annotation { "Feature Type Name" : "Feature", "Feature Type Description" : "" }
export const myFeature = defineFeature(function(context is Context, id is Id, definition is map)
    precondition{}
    {
        {
            var Q0;
            Q0=qCreatedBy(makeId("Front.planeOp"),FACE);
            var sketch = newSketch(context, id + "F0", { "sketchPlane" : qUnion([Q0])});
            skLineSegment(sketch, "E0.bottom", {"start": v(107, -79) * mm, "end": v(-107, -79) * mm});
            skLineSegment(sketch, "E0.top", {"start": v(107, 79) * mm, "end": v(-107, 79) * mm});
            skLineSegment(sketch, "E0.left", {"start": v(107, -79) * mm, "end": v(107, 79) * mm});
            skLineSegment(sketch, "E0.right", {"start": v(-107, -79) * mm, "end": v(-107, 79) * mm});
            skPoint(sketch, "E0.middle", {"position": v(0, 0) * mm});
            skSolve(sketch);
        }
        {
            var Q0;
            Q0=makeQuery(id+"F0.imprint","IMPRINT",FACE,{"disambiguationData":[TD([[makeQuery(id+"F0.imprint","IMPRINT",EDGE,{"derivedFrom":sQuery(id+"F0.wireOp",EDGE,"E0.bottom")}),-1.0]])]});
            extrude(context, id + "F1", {"entities" : qUnion([Q0]), "oppositeDirection" : true, "depth" : 6.2 * mm, "offsetDistance" : 25 * mm});
        }
        {
            var Q0;
            Q0=makeQuery(id+"F1.opExtrude","CAP_FACE",FACE,{"disambiguationData":[OSD([sQuery(id+"F0.wireOp",EDGE,"E0.bottom"),sQuery(id+"F0.wireOp",EDGE,"E0.top"),sQuery(id+"F0.wireOp",EDGE,"E0.left"),sQuery(id+"F0.wireOp",EDGE,"E0.right")])],"isStart":true});
            var sketch = newSketch(context, id + "F2", { "sketchPlane" : qUnion([Q0])});
            skLineSegment(sketch, "E1.bottom", {"start": v(98, -70) * mm, "end": v(-98, -70) * mm});
            skLineSegment(sketch, "E1.top", {"start": v(98, 70) * mm, "end": v(-98, 70) * mm});
            skLineSegment(sketch, "E1.left", {"start": v(98, -70) * mm, "end": v(98, 70) * mm});
            skLineSegment(sketch, "E1.right", {"start": v(-98, -70) * mm, "end": v(-98, 70) * mm});
            skPoint(sketch, "E1.middle", {"position": v(0, 0) * mm});
            skSolve(sketch);
        }
        {
            var Q0;
            Q0=makeQuery(id+"F2.imprint","IMPRINT",FACE,{"disambiguationData":[TD([[makeQuery(id+"F2.imprint","IMPRINT",EDGE,{"derivedFrom":sQuery(id+"F2.wireOp",EDGE,"E1.bottom")}),-1.0]])]});
            extrude(context, id + "F3", {"entities" : qUnion([Q0]), "operationType" : NewBodyOperationType.ADD, "depth" : 44 * mm, "offsetDistance" : 25 * mm});
        }
        {
            var Q0;
            Q0=makeQuery(id+"F1.opExtrude","SWEPT_FACE",FACE,{"disambiguationData":[OSD([sQuery(id+"F0.wireOp",EDGE,"E0.top")])]});
            var sketch = newSketch(context, id + "F4", { "sketchPlane" : qUnion([Q0])});
            skLineSegment(sketch, "E2", {"start": v(107, 0) * mm, "end": v(107, 0) * mm});
            skLineSegment(sketch, "E3", {"start": v(100.8, 6.2) * mm, "end": v(96.38, 6.2) * mm});
            skPoint(sketch, "E4.visualSharp", {"position": v(107, 6.2) * mm});
            skArc(sketch, "E4.filletArc", {"start": v(107, 0) * mm, "mid": v(105.18, 4.38) * mm, "end": v(100.8, 6.2) * mm});
            skLineSegment(sketch, "E5", {"start": v(96.38, 6.2) * mm, "end": v(-100.8, 6.2) * mm});
            skLineSegment(sketch, "E6", {"start": v(-107, 0) * mm, "end": v(-107, 0) * mm});
            skLineSegment(sketch, "E7", {"start": v(-107, 0) * mm, "end": v(107, 0) * mm});
            skPoint(sketch, "E8.visualSharp", {"position": v(-107, 6.2) * mm});
            skArc(sketch, "E8.filletArc", {"start": v(-100.8, 6.2) * mm, "mid": v(-105.18, 4.38) * mm, "end": v(-107, 0) * mm});
            skSolve(sketch);
        }
        {
            var Q0;
            {var subQ0=sQuery(id+"F4.wireOp",EDGE,"E4.filletArc");Q0=makeQuery(id+"F4.imprint","IMPRINT",FACE,{"disambiguationData":[TD([[makeQuery(id+"F4.imprint","IMPRINT",EDGE,{"derivedFrom":subQ0}),-1.0]])]});}
            var Q1;
            {var subQ0=sQuery(id+"F4.wireOp",EDGE,"E8.filletArc");Q1=makeQuery(id+"F4.imprint","IMPRINT",FACE,{"disambiguationData":[TD([[makeQuery(id+"F4.imprint","IMPRINT",EDGE,{"derivedFrom":subQ0}),-1.0]])]});}
            extrude(context, id + "F5", {"entities" : qUnion([Q0, Q1]), "operationType" : NewBodyOperationType.REMOVE, "oppositeDirection" : true, "depth" : 158 * mm, "offsetDistance" : 25 * mm});
        }
        {
            var Q0;
            Q0=makeQuery(id+"F3.opExtrude","CAP_FACE",FACE,{"disambiguationData":[OSD([sQuery(id+"F2.wireOp",EDGE,"E1.bottom"),sQuery(id+"F2.wireOp",EDGE,"E1.top"),sQuery(id+"F2.wireOp",EDGE,"E1.left"),sQuery(id+"F2.wireOp",EDGE,"E1.right")])],"isStart":false});
            var sketch = newSketch(context, id + "F6", { "sketchPlane" : qUnion([Q0])});
            skLineSegment(sketch, "E9.bottom", {"start": v(98, -70) * mm, "end": v(-98, -70) * mm});
            skLineSegment(sketch, "E9.top", {"start": v(98, 40) * mm, "end": v(-98, 40) * mm});
            skLineSegment(sketch, "E9.left", {"start": v(98, -70) * mm, "end": v(98, 40) * mm});
            skLineSegment(sketch, "E9.right", {"start": v(-98, -70) * mm, "end": v(-98, 40) * mm});
            skSolve(sketch);
        }
        {
            var Q0;
            Q0=makeQuery(id+"F6.imprint","IMPRINT",FACE,{"disambiguationData":[TD([[makeQuery(id+"F6.imprint","IMPRINT",EDGE,{"derivedFrom":sQuery(id+"F6.wireOp",EDGE,"E9.bottom")}),-1.0]])]});
            extrude(context, id + "F7", {"entities" : qUnion([Q0]), "operationType" : NewBodyOperationType.ADD, "depth" : 20 * mm, "offsetDistance" : 25 * mm});
        }
        {
            var Q0;
            Q0=makeQuery(id+"F7.boolean.opBoolean","MERGE",EDGE,{"derivedFrom":[makeQuery(id+"F3.opExtrude","SWEPT_EDGE",EDGE,{"disambiguationData":[OSD([sQuery(id+"F2.wireOp",EDGE,"E1.bottom"),sQuery(id+"F2.wireOp",EDGE,"E1.right")])]}),makeQuery(id+"F7.opExtrude","SWEPT_EDGE",EDGE,{"disambiguationData":[OSD([sQuery(id+"F6.wireOp",EDGE,"E9.bottom"),sQuery(id+"F6.wireOp",EDGE,"E9.right")])]})]});
            var Q1;
            Q1=makeQuery(id+"F7.boolean.opBoolean","MERGE",EDGE,{"derivedFrom":[makeQuery(id+"F3.opExtrude","SWEPT_EDGE",EDGE,{"disambiguationData":[OSD([sQuery(id+"F2.wireOp",EDGE,"E1.bottom"),sQuery(id+"F2.wireOp",EDGE,"E1.left")])]}),makeQuery(id+"F7.opExtrude","SWEPT_EDGE",EDGE,{"disambiguationData":[OSD([sQuery(id+"F6.wireOp",EDGE,"E9.bottom"),sQuery(id+"F6.wireOp",EDGE,"E9.left")])]})]});
            var Q2;
            Q2=makeQuery(id+"F3.opExtrude","SWEPT_EDGE",EDGE,{"disambiguationData":[OSD([sQuery(id+"F2.wireOp",EDGE,"E1.top"),sQuery(id+"F2.wireOp",EDGE,"E1.left")])]});
            var Q3;
            Q3=makeQuery(id+"F7.opExtrude","SWEPT_EDGE",EDGE,{"disambiguationData":[OSD([sQuery(id+"F2.wireOp",EDGE,"E1.left"),sQuery(id+"F6.wireOp",EDGE,"E9.top"),sQuery(id+"F6.wireOp",EDGE,"E9.left")])]});
            var Q4;
            Q4=makeQuery(id+"F3.opExtrude","SWEPT_EDGE",EDGE,{"disambiguationData":[OSD([sQuery(id+"F2.wireOp",EDGE,"E1.top"),sQuery(id+"F2.wireOp",EDGE,"E1.right")])]});
            var Q5;
            Q5=makeQuery(id+"F7.opExtrude","SWEPT_EDGE",EDGE,{"disambiguationData":[OSD([sQuery(id+"F2.wireOp",EDGE,"E1.right"),sQuery(id+"F6.wireOp",EDGE,"E9.top"),sQuery(id+"F6.wireOp",EDGE,"E9.right")])]});
            fillet(context, id + "F8", {"entities" : qUnion([Q0, Q1, Q2, Q3, Q4, Q5]), "radius" : 5 * mm, "tangentPropagation" : true, "allowEdgeOverflow" : false});
        }
        {
            var Q0;
            Q0=makeQuery(id+"F7.boolean.opBoolean","MERGE",FACE,{"derivedFrom":[makeQuery(id+"F3.opExtrude","SWEPT_FACE",FACE,{"disambiguationData":[OSD([sQuery(id+"F2.wireOp",EDGE,"E1.right")])]}),makeQuery(id+"F7.opExtrude","SWEPT_FACE",FACE,{"disambiguationData":[OSD([sQuery(id+"F6.wireOp",EDGE,"E9.right")])]})]});
            var sketch = newSketch(context, id + "F9", { "sketchPlane" : qUnion([Q0])});
            skLineSegment(sketch, "E10.bottom", {"start": v(7.5, -58) * mm, "end": v(19.5, -58) * mm});
            skLineSegment(sketch, "E10.top", {"start": v(7.5, -54) * mm, "end": v(19.5, -54) * mm});
            skLineSegment(sketch, "E10.left", {"start": v(7.5, -58) * mm, "end": v(7.5, -54) * mm});
            skLineSegment(sketch, "E10.right", {"start": v(19.5, -58) * mm, "end": v(19.5, -54) * mm});
            skLineSegment(sketch, "E11.0.1.0", {"start": v(7.5, -47) * mm, "end": v(19.5, -47) * mm});
            skLineSegment(sketch, "E11.0.1.1", {"start": v(7.5, -51) * mm, "end": v(19.5, -51) * mm});
            skLineSegment(sketch, "E11.0.1.2", {"start": v(19.5, -51) * mm, "end": v(19.5, -47) * mm});
            skLineSegment(sketch, "E11.0.1.3", {"start": v(7.5, -51) * mm, "end": v(7.5, -47) * mm});
            skLineSegment(sketch, "E11.0.2.0", {"start": v(7.5, -40) * mm, "end": v(19.5, -40) * mm});
            skLineSegment(sketch, "E11.0.2.1", {"start": v(7.5, -44) * mm, "end": v(19.5, -44) * mm});
            skLineSegment(sketch, "E11.0.2.2", {"start": v(19.5, -44) * mm, "end": v(19.5, -40) * mm});
            skLineSegment(sketch, "E11.0.2.3", {"start": v(7.5, -44) * mm, "end": v(7.5, -40) * mm});
            skLineSegment(sketch, "E11.0.3.0", {"start": v(7.5, -33) * mm, "end": v(19.5, -33) * mm});
            skLineSegment(sketch, "E11.0.3.1", {"start": v(7.5, -37) * mm, "end": v(19.5, -37) * mm});
            skLineSegment(sketch, "E11.0.3.2", {"start": v(19.5, -37) * mm, "end": v(19.5, -33) * mm});
            skLineSegment(sketch, "E11.0.3.3", {"start": v(7.5, -37) * mm, "end": v(7.5, -33) * mm});
            skLineSegment(sketch, "E11.0.4.0", {"start": v(7.5, -26) * mm, "end": v(19.5, -26) * mm});
            skLineSegment(sketch, "E11.0.4.1", {"start": v(7.5, -30) * mm, "end": v(19.5, -30) * mm});
            skLineSegment(sketch, "E11.0.4.2", {"start": v(19.5, -30) * mm, "end": v(19.5, -26) * mm});
            skLineSegment(sketch, "E11.0.4.3", {"start": v(7.5, -30) * mm, "end": v(7.5, -26) * mm});
            skLineSegment(sketch, "E11.0.5.0", {"start": v(7.5, -19) * mm, "end": v(19.5, -19) * mm});
            skLineSegment(sketch, "E11.0.5.1", {"start": v(7.5, -23) * mm, "end": v(19.5, -23) * mm});
            skLineSegment(sketch, "E11.0.5.2", {"start": v(19.5, -23) * mm, "end": v(19.5, -19) * mm});
            skLineSegment(sketch, "E11.0.5.3", {"start": v(7.5, -23) * mm, "end": v(7.5, -19) * mm});
            skLineSegment(sketch, "E11.0.6.0", {"start": v(7.5, -12) * mm, "end": v(19.5, -12) * mm});
            skLineSegment(sketch, "E11.0.6.1", {"start": v(7.5, -16) * mm, "end": v(19.5, -16) * mm});
            skLineSegment(sketch, "E11.0.6.2", {"start": v(19.5, -16) * mm, "end": v(19.5, -12) * mm});
            skLineSegment(sketch, "E11.0.6.3", {"start": v(7.5, -16) * mm, "end": v(7.5, -12) * mm});
            skLineSegment(sketch, "E11.0.7.0", {"start": v(7.5, -5) * mm, "end": v(19.5, -5) * mm});
            skLineSegment(sketch, "E11.0.7.1", {"start": v(7.5, -9) * mm, "end": v(19.5, -9) * mm});
            skLineSegment(sketch, "E11.0.7.2", {"start": v(19.5, -9) * mm, "end": v(19.5, -5) * mm});
            skLineSegment(sketch, "E11.0.7.3", {"start": v(7.5, -9) * mm, "end": v(7.5, -5) * mm});
            skLineSegment(sketch, "E11.0.8.0", {"start": v(7.5, 2) * mm, "end": v(19.5, 2) * mm});
            skLineSegment(sketch, "E11.0.8.1", {"start": v(7.5, -2) * mm, "end": v(19.5, -2) * mm});
            skLineSegment(sketch, "E11.0.8.2", {"start": v(19.5, -2) * mm, "end": v(19.5, 2) * mm});
            skLineSegment(sketch, "E11.0.8.3", {"start": v(7.5, -2) * mm, "end": v(7.5, 2) * mm});
            skLineSegment(sketch, "E11.0.9.0", {"start": v(7.5, 9) * mm, "end": v(19.5, 9) * mm});
            skLineSegment(sketch, "E11.0.9.1", {"start": v(7.5, 5) * mm, "end": v(19.5, 5) * mm});
            skLineSegment(sketch, "E11.0.9.2", {"start": v(19.5, 5) * mm, "end": v(19.5, 9) * mm});
            skLineSegment(sketch, "E11.0.9.3", {"start": v(7.5, 5) * mm, "end": v(7.5, 9) * mm});
            skLineSegment(sketch, "E11.0.10.0", {"start": v(7.5, 16) * mm, "end": v(19.5, 16) * mm});
            skLineSegment(sketch, "E11.0.10.1", {"start": v(7.5, 12) * mm, "end": v(19.5, 12) * mm});
            skLineSegment(sketch, "E11.0.10.2", {"start": v(19.5, 12) * mm, "end": v(19.5, 16) * mm});
            skLineSegment(sketch, "E11.0.10.3", {"start": v(7.5, 12) * mm, "end": v(7.5, 16) * mm});
            skLineSegment(sketch, "E11.0.11.0", {"start": v(7.5, 23) * mm, "end": v(19.5, 23) * mm});
            skLineSegment(sketch, "E11.0.11.1", {"start": v(7.5, 19) * mm, "end": v(19.5, 19) * mm});
            skLineSegment(sketch, "E11.0.11.2", {"start": v(19.5, 19) * mm, "end": v(19.5, 23) * mm});
            skLineSegment(sketch, "E11.0.11.3", {"start": v(7.5, 19) * mm, "end": v(7.5, 23) * mm});
            skLineSegment(sketch, "E11.0.13.0", {"start": v(7.5, 37) * mm, "end": v(19.5, 37) * mm});
            skLineSegment(sketch, "E11.0.13.1", {"start": v(7.5, 33) * mm, "end": v(19.5, 33) * mm});
            skLineSegment(sketch, "E11.0.13.2", {"start": v(19.5, 33) * mm, "end": v(19.5, 37) * mm});
            skLineSegment(sketch, "E11.0.13.3", {"start": v(7.5, 33) * mm, "end": v(7.5, 37) * mm});
            skLineSegment(sketch, "E11.0.14.0", {"start": v(7.5, 44) * mm, "end": v(19.5, 44) * mm});
            skLineSegment(sketch, "E11.0.14.1", {"start": v(7.5, 40) * mm, "end": v(19.5, 40) * mm});
            skLineSegment(sketch, "E11.0.14.2", {"start": v(19.5, 40) * mm, "end": v(19.5, 44) * mm});
            skLineSegment(sketch, "E11.0.14.3", {"start": v(7.5, 40) * mm, "end": v(7.5, 44) * mm});
            skLineSegment(sketch, "E11.0.15.0", {"start": v(7.5, 51) * mm, "end": v(19.5, 51) * mm});
            skLineSegment(sketch, "E11.0.15.1", {"start": v(7.5, 47) * mm, "end": v(19.5, 47) * mm});
            skLineSegment(sketch, "E11.0.15.2", {"start": v(19.5, 47) * mm, "end": v(19.5, 51) * mm});
            skLineSegment(sketch, "E11.0.15.3", {"start": v(7.5, 47) * mm, "end": v(7.5, 51) * mm});
            skLineSegment(sketch, "E11.0.16.0", {"start": v(7.5, 58) * mm, "end": v(19.5, 58) * mm});
            skLineSegment(sketch, "E11.0.16.1", {"start": v(7.5, 54) * mm, "end": v(19.5, 54) * mm});
            skLineSegment(sketch, "E11.0.16.2", {"start": v(19.5, 54) * mm, "end": v(19.5, 58) * mm});
            skLineSegment(sketch, "E11.0.16.3", {"start": v(7.5, 54) * mm, "end": v(7.5, 58) * mm});
            skLineSegment(sketch, "E11.1.0.0", {"start": v(24.5, -54) * mm, "end": v(36.5, -54) * mm});
            skLineSegment(sketch, "E11.1.0.1", {"start": v(24.5, -58) * mm, "end": v(36.5, -58) * mm});
            skLineSegment(sketch, "E11.1.0.2", {"start": v(36.5, -58) * mm, "end": v(36.5, -54) * mm});
            skLineSegment(sketch, "E11.1.0.3", {"start": v(24.5, -58) * mm, "end": v(24.5, -54) * mm});
            skLineSegment(sketch, "E11.1.1.0", {"start": v(24.5, -47) * mm, "end": v(36.5, -47) * mm});
            skLineSegment(sketch, "E11.1.1.1", {"start": v(24.5, -51) * mm, "end": v(36.5, -51) * mm});
            skLineSegment(sketch, "E11.1.1.2", {"start": v(36.5, -51) * mm, "end": v(36.5, -47) * mm});
            skLineSegment(sketch, "E11.1.1.3", {"start": v(24.5, -51) * mm, "end": v(24.5, -47) * mm});
            skLineSegment(sketch, "E11.1.2.0", {"start": v(24.5, -40) * mm, "end": v(36.5, -40) * mm});
            skLineSegment(sketch, "E11.1.2.1", {"start": v(24.5, -44) * mm, "end": v(36.5, -44) * mm});
            skLineSegment(sketch, "E11.1.2.2", {"start": v(36.5, -44) * mm, "end": v(36.5, -40) * mm});
            skLineSegment(sketch, "E11.1.2.3", {"start": v(24.5, -44) * mm, "end": v(24.5, -40) * mm});
            skLineSegment(sketch, "E11.1.3.0", {"start": v(24.5, -33) * mm, "end": v(36.5, -33) * mm});
            skLineSegment(sketch, "E11.1.3.1", {"start": v(24.5, -37) * mm, "end": v(36.5, -37) * mm});
            skLineSegment(sketch, "E11.1.3.2", {"start": v(36.5, -37) * mm, "end": v(36.5, -33) * mm});
            skLineSegment(sketch, "E11.1.3.3", {"start": v(24.5, -37) * mm, "end": v(24.5, -33) * mm});
            skLineSegment(sketch, "E11.1.4.0", {"start": v(24.5, -26) * mm, "end": v(36.5, -26) * mm});
            skLineSegment(sketch, "E11.1.4.1", {"start": v(24.5, -30) * mm, "end": v(36.5, -30) * mm});
            skLineSegment(sketch, "E11.1.4.2", {"start": v(36.5, -30) * mm, "end": v(36.5, -26) * mm});
            skLineSegment(sketch, "E11.1.4.3", {"start": v(24.5, -30) * mm, "end": v(24.5, -26) * mm});
            skLineSegment(sketch, "E11.1.5.0", {"start": v(24.5, -19) * mm, "end": v(36.5, -19) * mm});
            skLineSegment(sketch, "E11.1.5.1", {"start": v(24.5, -23) * mm, "end": v(36.5, -23) * mm});
            skLineSegment(sketch, "E11.1.5.2", {"start": v(36.5, -23) * mm, "end": v(36.5, -19) * mm});
            skLineSegment(sketch, "E11.1.5.3", {"start": v(24.5, -23) * mm, "end": v(24.5, -19) * mm});
            skLineSegment(sketch, "E11.1.6.0", {"start": v(24.5, -12) * mm, "end": v(36.5, -12) * mm});
            skLineSegment(sketch, "E11.1.6.1", {"start": v(24.5, -16) * mm, "end": v(36.5, -16) * mm});
            skLineSegment(sketch, "E11.1.6.2", {"start": v(36.5, -16) * mm, "end": v(36.5, -12) * mm});
            skLineSegment(sketch, "E11.1.6.3", {"start": v(24.5, -16) * mm, "end": v(24.5, -12) * mm});
            skLineSegment(sketch, "E11.1.7.0", {"start": v(24.5, -5) * mm, "end": v(36.5, -5) * mm});
            skLineSegment(sketch, "E11.1.7.1", {"start": v(24.5, -9) * mm, "end": v(36.5, -9) * mm});
            skLineSegment(sketch, "E11.1.7.2", {"start": v(36.5, -9) * mm, "end": v(36.5, -5) * mm});
            skLineSegment(sketch, "E11.1.7.3", {"start": v(24.5, -9) * mm, "end": v(24.5, -5) * mm});
            skLineSegment(sketch, "E11.1.8.0", {"start": v(24.5, 2) * mm, "end": v(36.5, 2) * mm});
            skLineSegment(sketch, "E11.1.8.1", {"start": v(24.5, -2) * mm, "end": v(36.5, -2) * mm});
            skLineSegment(sketch, "E11.1.8.2", {"start": v(36.5, -2) * mm, "end": v(36.5, 2) * mm});
            skLineSegment(sketch, "E11.1.8.3", {"start": v(24.5, -2) * mm, "end": v(24.5, 2) * mm});
            skLineSegment(sketch, "E11.1.9.0", {"start": v(24.5, 9) * mm, "end": v(36.5, 9) * mm});
            skLineSegment(sketch, "E11.1.9.1", {"start": v(24.5, 5) * mm, "end": v(36.5, 5) * mm});
            skLineSegment(sketch, "E11.1.9.2", {"start": v(36.5, 5) * mm, "end": v(36.5, 9) * mm});
            skLineSegment(sketch, "E11.1.9.3", {"start": v(24.5, 5) * mm, "end": v(24.5, 9) * mm});
            skLineSegment(sketch, "E11.1.10.0", {"start": v(24.5, 16) * mm, "end": v(36.5, 16) * mm});
            skLineSegment(sketch, "E11.1.10.1", {"start": v(24.5, 12) * mm, "end": v(36.5, 12) * mm});
            skLineSegment(sketch, "E11.1.10.2", {"start": v(36.5, 12) * mm, "end": v(36.5, 16) * mm});
            skLineSegment(sketch, "E11.1.10.3", {"start": v(24.5, 12) * mm, "end": v(24.5, 16) * mm});
            skLineSegment(sketch, "E11.1.11.0", {"start": v(24.5, 23) * mm, "end": v(36.5, 23) * mm});
            skLineSegment(sketch, "E11.1.11.1", {"start": v(24.5, 19) * mm, "end": v(36.5, 19) * mm});
            skLineSegment(sketch, "E11.1.11.2", {"start": v(36.5, 19) * mm, "end": v(36.5, 23) * mm});
            skLineSegment(sketch, "E11.1.11.3", {"start": v(24.5, 19) * mm, "end": v(24.5, 23) * mm});
            skLineSegment(sketch, "E11.1.13.0", {"start": v(24.5, 37) * mm, "end": v(36.5, 37) * mm});
            skLineSegment(sketch, "E11.1.13.1", {"start": v(24.5, 33) * mm, "end": v(36.5, 33) * mm});
            skLineSegment(sketch, "E11.1.13.2", {"start": v(36.5, 33) * mm, "end": v(36.5, 37) * mm});
            skLineSegment(sketch, "E11.1.13.3", {"start": v(24.5, 33) * mm, "end": v(24.5, 37) * mm});
            skLineSegment(sketch, "E11.1.14.0", {"start": v(24.5, 44) * mm, "end": v(36.5, 44) * mm});
            skLineSegment(sketch, "E11.1.14.1", {"start": v(24.5, 40) * mm, "end": v(36.5, 40) * mm});
            skLineSegment(sketch, "E11.1.14.2", {"start": v(36.5, 40) * mm, "end": v(36.5, 44) * mm});
            skLineSegment(sketch, "E11.1.14.3", {"start": v(24.5, 40) * mm, "end": v(24.5, 44) * mm});
            skLineSegment(sketch, "E11.1.15.0", {"start": v(24.5, 51) * mm, "end": v(36.5, 51) * mm});
            skLineSegment(sketch, "E11.1.15.1", {"start": v(24.5, 47) * mm, "end": v(36.5, 47) * mm});
            skLineSegment(sketch, "E11.1.15.2", {"start": v(36.5, 47) * mm, "end": v(36.5, 51) * mm});
            skLineSegment(sketch, "E11.1.15.3", {"start": v(24.5, 47) * mm, "end": v(24.5, 51) * mm});
            skLineSegment(sketch, "E11.1.16.0", {"start": v(24.5, 58) * mm, "end": v(36.5, 58) * mm});
            skLineSegment(sketch, "E11.1.16.1", {"start": v(24.5, 54) * mm, "end": v(36.5, 54) * mm});
            skLineSegment(sketch, "E11.1.16.2", {"start": v(36.5, 54) * mm, "end": v(36.5, 58) * mm});
            skLineSegment(sketch, "E11.1.16.3", {"start": v(24.5, 54) * mm, "end": v(24.5, 58) * mm});
            skLineSegment(sketch, "E11.direction1", {"start": v(7.5, -54) * mm, "end": v(24.5, -54) * mm, "construction": true});
            skLineSegment(sketch, "E11.direction2", {"start": v(7.5, -54) * mm, "end": v(7.5, -47) * mm, "construction": true});
            skSolve(sketch);
        }
        {
            var Q0;
            Q0=makeQuery(id+"F9.imprint","IMPRINT",FACE,{"disambiguationData":[TD([[makeQuery(id+"F9.imprint","IMPRINT",EDGE,{"derivedFrom":sQuery(id+"F9.wireOp",EDGE,"E10.bottom")}),1.0]])]});
            var Q1;
            Q1=makeQuery(id+"F9.imprint","IMPRINT",FACE,{"disambiguationData":[TD([[makeQuery(id+"F9.imprint","IMPRINT",EDGE,{"derivedFrom":sQuery(id+"F9.wireOp",EDGE,"E11.0.1.0")}),-1.0]])]});
            var Q2;
            Q2=makeQuery(id+"F9.imprint","IMPRINT",FACE,{"disambiguationData":[TD([[makeQuery(id+"F9.imprint","IMPRINT",EDGE,{"derivedFrom":sQuery(id+"F9.wireOp",EDGE,"E11.0.2.0")}),-1.0]])]});
            var Q3;
            Q3=makeQuery(id+"F9.imprint","IMPRINT",FACE,{"disambiguationData":[TD([[makeQuery(id+"F9.imprint","IMPRINT",EDGE,{"derivedFrom":sQuery(id+"F9.wireOp",EDGE,"E11.0.3.0")}),-1.0]])]});
            var Q4;
            Q4=makeQuery(id+"F9.imprint","IMPRINT",FACE,{"disambiguationData":[TD([[makeQuery(id+"F9.imprint","IMPRINT",EDGE,{"derivedFrom":sQuery(id+"F9.wireOp",EDGE,"E11.0.4.0")}),-1.0]])]});
            var Q5;
            Q5=makeQuery(id+"F9.imprint","IMPRINT",FACE,{"disambiguationData":[TD([[makeQuery(id+"F9.imprint","IMPRINT",EDGE,{"derivedFrom":sQuery(id+"F9.wireOp",EDGE,"E11.0.5.0")}),-1.0]])]});
            var Q6;
            Q6=makeQuery(id+"F9.imprint","IMPRINT",FACE,{"disambiguationData":[TD([[makeQuery(id+"F9.imprint","IMPRINT",EDGE,{"derivedFrom":sQuery(id+"F9.wireOp",EDGE,"E11.0.6.0")}),-1.0]])]});
            var Q7;
            Q7=makeQuery(id+"F9.imprint","IMPRINT",FACE,{"disambiguationData":[TD([[makeQuery(id+"F9.imprint","IMPRINT",EDGE,{"derivedFrom":sQuery(id+"F9.wireOp",EDGE,"E11.0.7.0")}),-1.0]])]});
            var Q8;
            Q8=makeQuery(id+"F9.imprint","IMPRINT",FACE,{"disambiguationData":[TD([[makeQuery(id+"F9.imprint","IMPRINT",EDGE,{"derivedFrom":sQuery(id+"F9.wireOp",EDGE,"E11.0.8.0")}),-1.0]])]});
            var Q9;
            Q9=makeQuery(id+"F9.imprint","IMPRINT",FACE,{"disambiguationData":[TD([[makeQuery(id+"F9.imprint","IMPRINT",EDGE,{"derivedFrom":sQuery(id+"F9.wireOp",EDGE,"E11.0.9.0")}),-1.0]])]});
            var Q10;
            Q10=makeQuery(id+"F9.imprint","IMPRINT",FACE,{"disambiguationData":[TD([[makeQuery(id+"F9.imprint","IMPRINT",EDGE,{"derivedFrom":sQuery(id+"F9.wireOp",EDGE,"E11.0.10.0")}),-1.0]])]});
            var Q11;
            Q11=makeQuery(id+"F9.imprint","IMPRINT",FACE,{"disambiguationData":[TD([[makeQuery(id+"F9.imprint","IMPRINT",EDGE,{"derivedFrom":sQuery(id+"F9.wireOp",EDGE,"E11.0.11.0")}),-1.0]])]});
            var Q12;
            Q12=makeQuery(id+"F9.imprint","IMPRINT",FACE,{"disambiguationData":[TD([[makeQuery(id+"F9.imprint","IMPRINT",EDGE,{"derivedFrom":sQuery(id+"F9.wireOp",EDGE,"E11.0.13.0")}),-1.0]])]});
            var Q13;
            Q13=makeQuery(id+"F9.imprint","IMPRINT",FACE,{"disambiguationData":[TD([[makeQuery(id+"F9.imprint","IMPRINT",EDGE,{"derivedFrom":sQuery(id+"F9.wireOp",EDGE,"E11.0.14.0")}),-1.0]])]});
            var Q14;
            Q14=makeQuery(id+"F9.imprint","IMPRINT",FACE,{"disambiguationData":[TD([[makeQuery(id+"F9.imprint","IMPRINT",EDGE,{"derivedFrom":sQuery(id+"F9.wireOp",EDGE,"E11.0.15.0")}),-1.0]])]});
            var Q15;
            Q15=makeQuery(id+"F9.imprint","IMPRINT",FACE,{"disambiguationData":[TD([[makeQuery(id+"F9.imprint","IMPRINT",EDGE,{"derivedFrom":sQuery(id+"F9.wireOp",EDGE,"E11.0.16.0")}),-1.0]])]});
            var Q16;
            Q16=makeQuery(id+"F9.imprint","IMPRINT",FACE,{"disambiguationData":[TD([[makeQuery(id+"F9.imprint","IMPRINT",EDGE,{"derivedFrom":sQuery(id+"F9.wireOp",EDGE,"E11.1.16.0")}),-1.0]])]});
            var Q17;
            Q17=makeQuery(id+"F9.imprint","IMPRINT",FACE,{"disambiguationData":[TD([[makeQuery(id+"F9.imprint","IMPRINT",EDGE,{"derivedFrom":sQuery(id+"F9.wireOp",EDGE,"E11.1.15.0")}),-1.0]])]});
            var Q18;
            Q18=makeQuery(id+"F9.imprint","IMPRINT",FACE,{"disambiguationData":[TD([[makeQuery(id+"F9.imprint","IMPRINT",EDGE,{"derivedFrom":sQuery(id+"F9.wireOp",EDGE,"E11.1.14.0")}),-1.0]])]});
            var Q19;
            Q19=makeQuery(id+"F9.imprint","IMPRINT",FACE,{"disambiguationData":[TD([[makeQuery(id+"F9.imprint","IMPRINT",EDGE,{"derivedFrom":sQuery(id+"F9.wireOp",EDGE,"E11.1.13.0")}),-1.0]])]});
            var Q20;
            Q20=makeQuery(id+"F9.imprint","IMPRINT",FACE,{"disambiguationData":[TD([[makeQuery(id+"F9.imprint","IMPRINT",EDGE,{"derivedFrom":sQuery(id+"F9.wireOp",EDGE,"E11.1.11.0")}),-1.0]])]});
            var Q21;
            Q21=makeQuery(id+"F9.imprint","IMPRINT",FACE,{"disambiguationData":[TD([[makeQuery(id+"F9.imprint","IMPRINT",EDGE,{"derivedFrom":sQuery(id+"F9.wireOp",EDGE,"E11.1.10.0")}),-1.0]])]});
            var Q22;
            Q22=makeQuery(id+"F9.imprint","IMPRINT",FACE,{"disambiguationData":[TD([[makeQuery(id+"F9.imprint","IMPRINT",EDGE,{"derivedFrom":sQuery(id+"F9.wireOp",EDGE,"E11.1.9.0")}),-1.0]])]});
            var Q23;
            Q23=makeQuery(id+"F9.imprint","IMPRINT",FACE,{"disambiguationData":[TD([[makeQuery(id+"F9.imprint","IMPRINT",EDGE,{"derivedFrom":sQuery(id+"F9.wireOp",EDGE,"E11.1.8.0")}),-1.0]])]});
            var Q24;
            Q24=makeQuery(id+"F9.imprint","IMPRINT",FACE,{"disambiguationData":[TD([[makeQuery(id+"F9.imprint","IMPRINT",EDGE,{"derivedFrom":sQuery(id+"F9.wireOp",EDGE,"E11.1.7.0")}),-1.0]])]});
            var Q25;
            Q25=makeQuery(id+"F9.imprint","IMPRINT",FACE,{"disambiguationData":[TD([[makeQuery(id+"F9.imprint","IMPRINT",EDGE,{"derivedFrom":sQuery(id+"F9.wireOp",EDGE,"E11.1.6.0")}),-1.0]])]});
            var Q26;
            Q26=makeQuery(id+"F9.imprint","IMPRINT",FACE,{"disambiguationData":[TD([[makeQuery(id+"F9.imprint","IMPRINT",EDGE,{"derivedFrom":sQuery(id+"F9.wireOp",EDGE,"E11.1.5.0")}),-1.0]])]});
            var Q27;
            Q27=makeQuery(id+"F9.imprint","IMPRINT",FACE,{"disambiguationData":[TD([[makeQuery(id+"F9.imprint","IMPRINT",EDGE,{"derivedFrom":sQuery(id+"F9.wireOp",EDGE,"E11.1.4.0")}),-1.0]])]});
            var Q28;
            Q28=makeQuery(id+"F9.imprint","IMPRINT",FACE,{"disambiguationData":[TD([[makeQuery(id+"F9.imprint","IMPRINT",EDGE,{"derivedFrom":sQuery(id+"F9.wireOp",EDGE,"E11.1.3.0")}),-1.0]])]});
            var Q29;
            Q29=makeQuery(id+"F9.imprint","IMPRINT",FACE,{"disambiguationData":[TD([[makeQuery(id+"F9.imprint","IMPRINT",EDGE,{"derivedFrom":sQuery(id+"F9.wireOp",EDGE,"E11.1.2.0")}),-1.0]])]});
            var Q30;
            Q30=makeQuery(id+"F9.imprint","IMPRINT",FACE,{"disambiguationData":[TD([[makeQuery(id+"F9.imprint","IMPRINT",EDGE,{"derivedFrom":sQuery(id+"F9.wireOp",EDGE,"E11.1.1.0")}),-1.0]])]});
            var Q31;
            Q31=makeQuery(id+"F9.imprint","IMPRINT",FACE,{"disambiguationData":[TD([[makeQuery(id+"F9.imprint","IMPRINT",EDGE,{"derivedFrom":sQuery(id+"F9.wireOp",EDGE,"E11.1.0.0")}),-1.0]])]});
            extrude(context, id + "F10", {"entities" : qUnion([Q0, Q1, Q2, Q3, Q4, Q5, Q6, Q7, Q8, Q9, Q10, Q11, Q12, Q13, Q14, Q15, Q16, Q17, Q18, Q19, Q20, Q21, Q22, Q23, Q24, Q25, Q26, Q27, Q28, Q29, Q30, Q31]), "operationType" : NewBodyOperationType.REMOVE, "oppositeDirection" : true, "depth" : 10 * mm, "offsetDistance" : 25 * mm});
        }
        {
            var Q0;
            Q0=makeQuery(id+"F7.boolean.opBoolean","MERGE",FACE,{"derivedFrom":[makeQuery(id+"F3.opExtrude","SWEPT_FACE",FACE,{"disambiguationData":[OSD([sQuery(id+"F2.wireOp",EDGE,"E1.left")])]}),makeQuery(id+"F7.opExtrude","SWEPT_FACE",FACE,{"disambiguationData":[OSD([sQuery(id+"F6.wireOp",EDGE,"E9.left")])]})]});
            var sketch = newSketch(context, id + "F11", { "sketchPlane" : qUnion([Q0])});
            skLineSegment(sketch, "E12.bottom", {"start": v(-7.5, 58) * mm, "end": v(-19.5, 58) * mm});
            skLineSegment(sketch, "E12.top", {"start": v(-7.5, 54) * mm, "end": v(-19.5, 54) * mm});
            skLineSegment(sketch, "E12.left", {"start": v(-7.5, 58) * mm, "end": v(-7.5, 54) * mm});
            skLineSegment(sketch, "E12.right", {"start": v(-19.5, 58) * mm, "end": v(-19.5, 54) * mm});
            skLineSegment(sketch, "E13.0.1.0", {"start": v(-7.5, 51) * mm, "end": v(-7.5, 47) * mm});
            skLineSegment(sketch, "E13.0.1.1", {"start": v(-7.5, 51) * mm, "end": v(-19.5, 51) * mm});
            skLineSegment(sketch, "E13.0.1.2", {"start": v(-7.5, 47) * mm, "end": v(-19.5, 47) * mm});
            skLineSegment(sketch, "E13.0.1.3", {"start": v(-19.5, 51) * mm, "end": v(-19.5, 47) * mm});
            skLineSegment(sketch, "E13.0.2.0", {"start": v(-7.5, 44) * mm, "end": v(-7.5, 40) * mm});
            skLineSegment(sketch, "E13.0.2.1", {"start": v(-7.5, 44) * mm, "end": v(-19.5, 44) * mm});
            skLineSegment(sketch, "E13.0.2.2", {"start": v(-7.5, 40) * mm, "end": v(-19.5, 40) * mm});
            skLineSegment(sketch, "E13.0.2.3", {"start": v(-19.5, 44) * mm, "end": v(-19.5, 40) * mm});
            skLineSegment(sketch, "E13.0.3.0", {"start": v(-7.5, 37) * mm, "end": v(-7.5, 33) * mm});
            skLineSegment(sketch, "E13.0.3.1", {"start": v(-7.5, 37) * mm, "end": v(-19.5, 37) * mm});
            skLineSegment(sketch, "E13.0.3.2", {"start": v(-7.5, 33) * mm, "end": v(-19.5, 33) * mm});
            skLineSegment(sketch, "E13.0.3.3", {"start": v(-19.5, 37) * mm, "end": v(-19.5, 33) * mm});
            skLineSegment(sketch, "E13.0.5.0", {"start": v(-7.5, 23) * mm, "end": v(-7.5, 19) * mm});
            skLineSegment(sketch, "E13.0.5.1", {"start": v(-7.5, 23) * mm, "end": v(-19.5, 23) * mm});
            skLineSegment(sketch, "E13.0.5.2", {"start": v(-7.5, 19) * mm, "end": v(-19.5, 19) * mm});
            skLineSegment(sketch, "E13.0.5.3", {"start": v(-19.5, 23) * mm, "end": v(-19.5, 19) * mm});
            skLineSegment(sketch, "E13.0.6.0", {"start": v(-7.5, 16) * mm, "end": v(-7.5, 12) * mm});
            skLineSegment(sketch, "E13.0.6.1", {"start": v(-7.5, 16) * mm, "end": v(-19.5, 16) * mm});
            skLineSegment(sketch, "E13.0.6.2", {"start": v(-7.5, 12) * mm, "end": v(-19.5, 12) * mm});
            skLineSegment(sketch, "E13.0.6.3", {"start": v(-19.5, 16) * mm, "end": v(-19.5, 12) * mm});
            skLineSegment(sketch, "E13.0.7.0", {"start": v(-7.5, 9) * mm, "end": v(-7.5, 5) * mm});
            skLineSegment(sketch, "E13.0.7.1", {"start": v(-7.5, 9) * mm, "end": v(-19.5, 9) * mm});
            skLineSegment(sketch, "E13.0.7.2", {"start": v(-7.5, 5) * mm, "end": v(-19.5, 5) * mm});
            skLineSegment(sketch, "E13.0.7.3", {"start": v(-19.5, 9) * mm, "end": v(-19.5, 5) * mm});
            skLineSegment(sketch, "E13.0.8.0", {"start": v(-7.5, 2) * mm, "end": v(-7.5, -2) * mm});
            skLineSegment(sketch, "E13.0.8.1", {"start": v(-7.5, 2) * mm, "end": v(-19.5, 2) * mm});
            skLineSegment(sketch, "E13.0.8.2", {"start": v(-7.5, -2) * mm, "end": v(-19.5, -2) * mm});
            skLineSegment(sketch, "E13.0.8.3", {"start": v(-19.5, 2) * mm, "end": v(-19.5, -2) * mm});
            skLineSegment(sketch, "E13.0.9.0", {"start": v(-7.5, -5) * mm, "end": v(-7.5, -9) * mm});
            skLineSegment(sketch, "E13.0.9.1", {"start": v(-7.5, -5) * mm, "end": v(-19.5, -5) * mm});
            skLineSegment(sketch, "E13.0.9.2", {"start": v(-7.5, -9) * mm, "end": v(-19.5, -9) * mm});
            skLineSegment(sketch, "E13.0.9.3", {"start": v(-19.5, -5) * mm, "end": v(-19.5, -9) * mm});
            skLineSegment(sketch, "E13.0.10.0", {"start": v(-7.5, -12) * mm, "end": v(-7.5, -16) * mm});
            skLineSegment(sketch, "E13.0.10.1", {"start": v(-7.5, -12) * mm, "end": v(-19.5, -12) * mm});
            skLineSegment(sketch, "E13.0.10.2", {"start": v(-7.5, -16) * mm, "end": v(-19.5, -16) * mm});
            skLineSegment(sketch, "E13.0.10.3", {"start": v(-19.5, -12) * mm, "end": v(-19.5, -16) * mm});
            skLineSegment(sketch, "E13.0.11.0", {"start": v(-7.5, -19) * mm, "end": v(-7.5, -23) * mm});
            skLineSegment(sketch, "E13.0.11.1", {"start": v(-7.5, -19) * mm, "end": v(-19.5, -19) * mm});
            skLineSegment(sketch, "E13.0.11.2", {"start": v(-7.5, -23) * mm, "end": v(-19.5, -23) * mm});
            skLineSegment(sketch, "E13.0.11.3", {"start": v(-19.5, -19) * mm, "end": v(-19.5, -23) * mm});
            skLineSegment(sketch, "E13.0.12.0", {"start": v(-7.5, -26) * mm, "end": v(-7.5, -30) * mm});
            skLineSegment(sketch, "E13.0.12.1", {"start": v(-7.5, -26) * mm, "end": v(-19.5, -26) * mm});
            skLineSegment(sketch, "E13.0.12.2", {"start": v(-7.5, -30) * mm, "end": v(-19.5, -30) * mm});
            skLineSegment(sketch, "E13.0.12.3", {"start": v(-19.5, -26) * mm, "end": v(-19.5, -30) * mm});
            skLineSegment(sketch, "E13.0.13.0", {"start": v(-7.5, -33) * mm, "end": v(-7.5, -37) * mm});
            skLineSegment(sketch, "E13.0.13.1", {"start": v(-7.5, -33) * mm, "end": v(-19.5, -33) * mm});
            skLineSegment(sketch, "E13.0.13.2", {"start": v(-7.5, -37) * mm, "end": v(-19.5, -37) * mm});
            skLineSegment(sketch, "E13.0.13.3", {"start": v(-19.5, -33) * mm, "end": v(-19.5, -37) * mm});
            skLineSegment(sketch, "E13.0.14.0", {"start": v(-7.5, -40) * mm, "end": v(-7.5, -44) * mm});
            skLineSegment(sketch, "E13.0.14.1", {"start": v(-7.5, -40) * mm, "end": v(-19.5, -40) * mm});
            skLineSegment(sketch, "E13.0.14.2", {"start": v(-7.5, -44) * mm, "end": v(-19.5, -44) * mm});
            skLineSegment(sketch, "E13.0.14.3", {"start": v(-19.5, -40) * mm, "end": v(-19.5, -44) * mm});
            skLineSegment(sketch, "E13.0.15.0", {"start": v(-7.5, -47) * mm, "end": v(-7.5, -51) * mm});
            skLineSegment(sketch, "E13.0.15.1", {"start": v(-7.5, -47) * mm, "end": v(-19.5, -47) * mm});
            skLineSegment(sketch, "E13.0.15.2", {"start": v(-7.5, -51) * mm, "end": v(-19.5, -51) * mm});
            skLineSegment(sketch, "E13.0.15.3", {"start": v(-19.5, -47) * mm, "end": v(-19.5, -51) * mm});
            skLineSegment(sketch, "E13.0.16.0", {"start": v(-7.5, -54) * mm, "end": v(-7.5, -58) * mm});
            skLineSegment(sketch, "E13.0.16.1", {"start": v(-7.5, -54) * mm, "end": v(-19.5, -54) * mm});
            skLineSegment(sketch, "E13.0.16.2", {"start": v(-7.5, -58) * mm, "end": v(-19.5, -58) * mm});
            skLineSegment(sketch, "E13.0.16.3", {"start": v(-19.5, -54) * mm, "end": v(-19.5, -58) * mm});
            skLineSegment(sketch, "E13.1.0.0", {"start": v(-24.5, 58) * mm, "end": v(-24.5, 54) * mm});
            skLineSegment(sketch, "E13.1.0.1", {"start": v(-24.5, 58) * mm, "end": v(-36.5, 58) * mm});
            skLineSegment(sketch, "E13.1.0.2", {"start": v(-24.5, 54) * mm, "end": v(-36.5, 54) * mm});
            skLineSegment(sketch, "E13.1.0.3", {"start": v(-36.5, 58) * mm, "end": v(-36.5, 54) * mm});
            skLineSegment(sketch, "E13.1.1.0", {"start": v(-24.5, 51) * mm, "end": v(-24.5, 47) * mm});
            skLineSegment(sketch, "E13.1.1.1", {"start": v(-24.5, 51) * mm, "end": v(-36.5, 51) * mm});
            skLineSegment(sketch, "E13.1.1.2", {"start": v(-24.5, 47) * mm, "end": v(-36.5, 47) * mm});
            skLineSegment(sketch, "E13.1.1.3", {"start": v(-36.5, 51) * mm, "end": v(-36.5, 47) * mm});
            skLineSegment(sketch, "E13.1.2.0", {"start": v(-24.5, 44) * mm, "end": v(-24.5, 40) * mm});
            skLineSegment(sketch, "E13.1.2.1", {"start": v(-24.5, 44) * mm, "end": v(-36.5, 44) * mm});
            skLineSegment(sketch, "E13.1.2.2", {"start": v(-24.5, 40) * mm, "end": v(-36.5, 40) * mm});
            skLineSegment(sketch, "E13.1.2.3", {"start": v(-36.5, 44) * mm, "end": v(-36.5, 40) * mm});
            skLineSegment(sketch, "E13.1.3.0", {"start": v(-24.5, 37) * mm, "end": v(-24.5, 33) * mm});
            skLineSegment(sketch, "E13.1.3.1", {"start": v(-24.5, 37) * mm, "end": v(-36.5, 37) * mm});
            skLineSegment(sketch, "E13.1.3.2", {"start": v(-24.5, 33) * mm, "end": v(-36.5, 33) * mm});
            skLineSegment(sketch, "E13.1.3.3", {"start": v(-36.5, 37) * mm, "end": v(-36.5, 33) * mm});
            skLineSegment(sketch, "E13.1.5.0", {"start": v(-24.5, 23) * mm, "end": v(-24.5, 19) * mm});
            skLineSegment(sketch, "E13.1.5.1", {"start": v(-24.5, 23) * mm, "end": v(-36.5, 23) * mm});
            skLineSegment(sketch, "E13.1.5.2", {"start": v(-24.5, 19) * mm, "end": v(-36.5, 19) * mm});
            skLineSegment(sketch, "E13.1.5.3", {"start": v(-36.5, 23) * mm, "end": v(-36.5, 19) * mm});
            skLineSegment(sketch, "E13.1.6.0", {"start": v(-24.5, 16) * mm, "end": v(-24.5, 12) * mm});
            skLineSegment(sketch, "E13.1.6.1", {"start": v(-24.5, 16) * mm, "end": v(-36.5, 16) * mm});
            skLineSegment(sketch, "E13.1.6.2", {"start": v(-24.5, 12) * mm, "end": v(-36.5, 12) * mm});
            skLineSegment(sketch, "E13.1.6.3", {"start": v(-36.5, 16) * mm, "end": v(-36.5, 12) * mm});
            skLineSegment(sketch, "E13.1.7.0", {"start": v(-24.5, 9) * mm, "end": v(-24.5, 5) * mm});
            skLineSegment(sketch, "E13.1.7.1", {"start": v(-24.5, 9) * mm, "end": v(-36.5, 9) * mm});
            skLineSegment(sketch, "E13.1.7.2", {"start": v(-24.5, 5) * mm, "end": v(-36.5, 5) * mm});
            skLineSegment(sketch, "E13.1.7.3", {"start": v(-36.5, 9) * mm, "end": v(-36.5, 5) * mm});
            skLineSegment(sketch, "E13.1.8.0", {"start": v(-24.5, 2) * mm, "end": v(-24.5, -2) * mm});
            skLineSegment(sketch, "E13.1.8.1", {"start": v(-24.5, 2) * mm, "end": v(-36.5, 2) * mm});
            skLineSegment(sketch, "E13.1.8.2", {"start": v(-24.5, -2) * mm, "end": v(-36.5, -2) * mm});
            skLineSegment(sketch, "E13.1.8.3", {"start": v(-36.5, 2) * mm, "end": v(-36.5, -2) * mm});
            skLineSegment(sketch, "E13.1.9.0", {"start": v(-24.5, -5) * mm, "end": v(-24.5, -9) * mm});
            skLineSegment(sketch, "E13.1.9.1", {"start": v(-24.5, -5) * mm, "end": v(-36.5, -5) * mm});
            skLineSegment(sketch, "E13.1.9.2", {"start": v(-24.5, -9) * mm, "end": v(-36.5, -9) * mm});
            skLineSegment(sketch, "E13.1.9.3", {"start": v(-36.5, -5) * mm, "end": v(-36.5, -9) * mm});
            skLineSegment(sketch, "E13.1.10.0", {"start": v(-24.5, -12) * mm, "end": v(-24.5, -16) * mm});
            skLineSegment(sketch, "E13.1.10.1", {"start": v(-24.5, -12) * mm, "end": v(-36.5, -12) * mm});
            skLineSegment(sketch, "E13.1.10.2", {"start": v(-24.5, -16) * mm, "end": v(-36.5, -16) * mm});
            skLineSegment(sketch, "E13.1.10.3", {"start": v(-36.5, -12) * mm, "end": v(-36.5, -16) * mm});
            skLineSegment(sketch, "E13.1.11.0", {"start": v(-24.5, -19) * mm, "end": v(-24.5, -23) * mm});
            skLineSegment(sketch, "E13.1.11.1", {"start": v(-24.5, -19) * mm, "end": v(-36.5, -19) * mm});
            skLineSegment(sketch, "E13.1.11.2", {"start": v(-24.5, -23) * mm, "end": v(-36.5, -23) * mm});
            skLineSegment(sketch, "E13.1.11.3", {"start": v(-36.5, -19) * mm, "end": v(-36.5, -23) * mm});
            skLineSegment(sketch, "E13.1.12.0", {"start": v(-24.5, -26) * mm, "end": v(-24.5, -30) * mm});
            skLineSegment(sketch, "E13.1.12.1", {"start": v(-24.5, -26) * mm, "end": v(-36.5, -26) * mm});
            skLineSegment(sketch, "E13.1.12.2", {"start": v(-24.5, -30) * mm, "end": v(-36.5, -30) * mm});
            skLineSegment(sketch, "E13.1.12.3", {"start": v(-36.5, -26) * mm, "end": v(-36.5, -30) * mm});
            skLineSegment(sketch, "E13.1.13.0", {"start": v(-24.5, -33) * mm, "end": v(-24.5, -37) * mm});
            skLineSegment(sketch, "E13.1.13.1", {"start": v(-24.5, -33) * mm, "end": v(-36.5, -33) * mm});
            skLineSegment(sketch, "E13.1.13.2", {"start": v(-24.5, -37) * mm, "end": v(-36.5, -37) * mm});
            skLineSegment(sketch, "E13.1.13.3", {"start": v(-36.5, -33) * mm, "end": v(-36.5, -37) * mm});
            skLineSegment(sketch, "E13.1.14.0", {"start": v(-24.5, -40) * mm, "end": v(-24.5, -44) * mm});
            skLineSegment(sketch, "E13.1.14.1", {"start": v(-24.5, -40) * mm, "end": v(-36.5, -40) * mm});
            skLineSegment(sketch, "E13.1.14.2", {"start": v(-24.5, -44) * mm, "end": v(-36.5, -44) * mm});
            skLineSegment(sketch, "E13.1.14.3", {"start": v(-36.5, -40) * mm, "end": v(-36.5, -44) * mm});
            skLineSegment(sketch, "E13.1.15.0", {"start": v(-24.5, -47) * mm, "end": v(-24.5, -51) * mm});
            skLineSegment(sketch, "E13.1.15.1", {"start": v(-24.5, -47) * mm, "end": v(-36.5, -47) * mm});
            skLineSegment(sketch, "E13.1.15.2", {"start": v(-24.5, -51) * mm, "end": v(-36.5, -51) * mm});
            skLineSegment(sketch, "E13.1.15.3", {"start": v(-36.5, -47) * mm, "end": v(-36.5, -51) * mm});
            skLineSegment(sketch, "E13.1.16.0", {"start": v(-24.5, -54) * mm, "end": v(-24.5, -58) * mm});
            skLineSegment(sketch, "E13.1.16.1", {"start": v(-24.5, -54) * mm, "end": v(-36.5, -54) * mm});
            skLineSegment(sketch, "E13.1.16.2", {"start": v(-24.5, -58) * mm, "end": v(-36.5, -58) * mm});
            skLineSegment(sketch, "E13.1.16.3", {"start": v(-36.5, -54) * mm, "end": v(-36.5, -58) * mm});
            skLineSegment(sketch, "E13.direction1", {"start": v(-7.5, 54) * mm, "end": v(-24.5, 54) * mm, "construction": true});
            skLineSegment(sketch, "E13.direction2", {"start": v(-7.5, 54) * mm, "end": v(-7.5, 47) * mm, "construction": true});
            skSolve(sketch);
        }
        {
            var Q0;
            Q0=makeQuery(id+"F11.imprint","IMPRINT",FACE,{"disambiguationData":[TD([[makeQuery(id+"F11.imprint","IMPRINT",EDGE,{"derivedFrom":sQuery(id+"F11.wireOp",EDGE,"E12.bottom")}),1.0]])]});
            var Q1;
            Q1=makeQuery(id+"F11.imprint","IMPRINT",FACE,{"disambiguationData":[TD([[makeQuery(id+"F11.imprint","IMPRINT",EDGE,{"derivedFrom":sQuery(id+"F11.wireOp",EDGE,"E13.0.1.0")}),-1.0]])]});
            var Q2;
            Q2=makeQuery(id+"F11.imprint","IMPRINT",FACE,{"disambiguationData":[TD([[makeQuery(id+"F11.imprint","IMPRINT",EDGE,{"derivedFrom":sQuery(id+"F11.wireOp",EDGE,"E13.0.2.0")}),-1.0]])]});
            var Q3;
            Q3=makeQuery(id+"F11.imprint","IMPRINT",FACE,{"disambiguationData":[TD([[makeQuery(id+"F11.imprint","IMPRINT",EDGE,{"derivedFrom":sQuery(id+"F11.wireOp",EDGE,"E13.0.3.0")}),-1.0]])]});
            var Q4;
            Q4=makeQuery(id+"F11.imprint","IMPRINT",FACE,{"disambiguationData":[TD([[makeQuery(id+"F11.imprint","IMPRINT",EDGE,{"derivedFrom":sQuery(id+"F11.wireOp",EDGE,"E13.1.0.0")}),-1.0]])]});
            var Q5;
            Q5=makeQuery(id+"F11.imprint","IMPRINT",FACE,{"disambiguationData":[TD([[makeQuery(id+"F11.imprint","IMPRINT",EDGE,{"derivedFrom":sQuery(id+"F11.wireOp",EDGE,"E13.1.1.0")}),-1.0]])]});
            var Q6;
            Q6=makeQuery(id+"F11.imprint","IMPRINT",FACE,{"disambiguationData":[TD([[makeQuery(id+"F11.imprint","IMPRINT",EDGE,{"derivedFrom":sQuery(id+"F11.wireOp",EDGE,"E13.1.2.0")}),-1.0]])]});
            var Q7;
            Q7=makeQuery(id+"F11.imprint","IMPRINT",FACE,{"disambiguationData":[TD([[makeQuery(id+"F11.imprint","IMPRINT",EDGE,{"derivedFrom":sQuery(id+"F11.wireOp",EDGE,"E13.1.3.0")}),-1.0]])]});
            var Q8;
            Q8=makeQuery(id+"F11.imprint","IMPRINT",FACE,{"disambiguationData":[TD([[makeQuery(id+"F11.imprint","IMPRINT",EDGE,{"derivedFrom":sQuery(id+"F11.wireOp",EDGE,"E13.0.5.0")}),-1.0]])]});
            var Q9;
            Q9=makeQuery(id+"F11.imprint","IMPRINT",FACE,{"disambiguationData":[TD([[makeQuery(id+"F11.imprint","IMPRINT",EDGE,{"derivedFrom":sQuery(id+"F11.wireOp",EDGE,"E13.0.6.0")}),-1.0]])]});
            var Q10;
            Q10=makeQuery(id+"F11.imprint","IMPRINT",FACE,{"disambiguationData":[TD([[makeQuery(id+"F11.imprint","IMPRINT",EDGE,{"derivedFrom":sQuery(id+"F11.wireOp",EDGE,"E13.0.7.0")}),-1.0]])]});
            var Q11;
            Q11=makeQuery(id+"F11.imprint","IMPRINT",FACE,{"disambiguationData":[TD([[makeQuery(id+"F11.imprint","IMPRINT",EDGE,{"derivedFrom":sQuery(id+"F11.wireOp",EDGE,"E13.0.8.0")}),-1.0]])]});
            var Q12;
            Q12=makeQuery(id+"F11.imprint","IMPRINT",FACE,{"disambiguationData":[TD([[makeQuery(id+"F11.imprint","IMPRINT",EDGE,{"derivedFrom":sQuery(id+"F11.wireOp",EDGE,"E13.0.9.0")}),-1.0]])]});
            var Q13;
            Q13=makeQuery(id+"F11.imprint","IMPRINT",FACE,{"disambiguationData":[TD([[makeQuery(id+"F11.imprint","IMPRINT",EDGE,{"derivedFrom":sQuery(id+"F11.wireOp",EDGE,"E13.0.10.0")}),-1.0]])]});
            var Q14;
            Q14=makeQuery(id+"F11.imprint","IMPRINT",FACE,{"disambiguationData":[TD([[makeQuery(id+"F11.imprint","IMPRINT",EDGE,{"derivedFrom":sQuery(id+"F11.wireOp",EDGE,"E13.0.11.0")}),-1.0]])]});
            var Q15;
            Q15=makeQuery(id+"F11.imprint","IMPRINT",FACE,{"disambiguationData":[TD([[makeQuery(id+"F11.imprint","IMPRINT",EDGE,{"derivedFrom":sQuery(id+"F11.wireOp",EDGE,"E13.0.12.0")}),-1.0]])]});
            var Q16;
            Q16=makeQuery(id+"F11.imprint","IMPRINT",FACE,{"disambiguationData":[TD([[makeQuery(id+"F11.imprint","IMPRINT",EDGE,{"derivedFrom":sQuery(id+"F11.wireOp",EDGE,"E13.0.13.0")}),-1.0]])]});
            var Q17;
            Q17=makeQuery(id+"F11.imprint","IMPRINT",FACE,{"disambiguationData":[TD([[makeQuery(id+"F11.imprint","IMPRINT",EDGE,{"derivedFrom":sQuery(id+"F11.wireOp",EDGE,"E13.0.14.0")}),-1.0]])]});
            var Q18;
            Q18=makeQuery(id+"F11.imprint","IMPRINT",FACE,{"disambiguationData":[TD([[makeQuery(id+"F11.imprint","IMPRINT",EDGE,{"derivedFrom":sQuery(id+"F11.wireOp",EDGE,"E13.0.15.0")}),-1.0]])]});
            var Q19;
            Q19=makeQuery(id+"F11.imprint","IMPRINT",FACE,{"disambiguationData":[TD([[makeQuery(id+"F11.imprint","IMPRINT",EDGE,{"derivedFrom":sQuery(id+"F11.wireOp",EDGE,"E13.0.16.0")}),-1.0]])]});
            var Q20;
            Q20=makeQuery(id+"F11.imprint","IMPRINT",FACE,{"disambiguationData":[TD([[makeQuery(id+"F11.imprint","IMPRINT",EDGE,{"derivedFrom":sQuery(id+"F11.wireOp",EDGE,"E13.1.5.0")}),-1.0]])]});
            var Q21;
            Q21=makeQuery(id+"F11.imprint","IMPRINT",FACE,{"disambiguationData":[TD([[makeQuery(id+"F11.imprint","IMPRINT",EDGE,{"derivedFrom":sQuery(id+"F11.wireOp",EDGE,"E13.1.6.0")}),-1.0]])]});
            var Q22;
            Q22=makeQuery(id+"F11.imprint","IMPRINT",FACE,{"disambiguationData":[TD([[makeQuery(id+"F11.imprint","IMPRINT",EDGE,{"derivedFrom":sQuery(id+"F11.wireOp",EDGE,"E13.1.7.0")}),-1.0]])]});
            var Q23;
            Q23=makeQuery(id+"F11.imprint","IMPRINT",FACE,{"disambiguationData":[TD([[makeQuery(id+"F11.imprint","IMPRINT",EDGE,{"derivedFrom":sQuery(id+"F11.wireOp",EDGE,"E13.1.8.0")}),-1.0]])]});
            var Q24;
            Q24=makeQuery(id+"F11.imprint","IMPRINT",FACE,{"disambiguationData":[TD([[makeQuery(id+"F11.imprint","IMPRINT",EDGE,{"derivedFrom":sQuery(id+"F11.wireOp",EDGE,"E13.1.9.0")}),-1.0]])]});
            var Q25;
            Q25=makeQuery(id+"F11.imprint","IMPRINT",FACE,{"disambiguationData":[TD([[makeQuery(id+"F11.imprint","IMPRINT",EDGE,{"derivedFrom":sQuery(id+"F11.wireOp",EDGE,"E13.1.10.0")}),-1.0]])]});
            var Q26;
            Q26=makeQuery(id+"F11.imprint","IMPRINT",FACE,{"disambiguationData":[TD([[makeQuery(id+"F11.imprint","IMPRINT",EDGE,{"derivedFrom":sQuery(id+"F11.wireOp",EDGE,"E13.1.11.0")}),-1.0]])]});
            var Q27;
            Q27=makeQuery(id+"F11.imprint","IMPRINT",FACE,{"disambiguationData":[TD([[makeQuery(id+"F11.imprint","IMPRINT",EDGE,{"derivedFrom":sQuery(id+"F11.wireOp",EDGE,"E13.1.12.0")}),-1.0]])]});
            var Q28;
            Q28=makeQuery(id+"F11.imprint","IMPRINT",FACE,{"disambiguationData":[TD([[makeQuery(id+"F11.imprint","IMPRINT",EDGE,{"derivedFrom":sQuery(id+"F11.wireOp",EDGE,"E13.1.13.0")}),-1.0]])]});
            var Q29;
            Q29=makeQuery(id+"F11.imprint","IMPRINT",FACE,{"disambiguationData":[TD([[makeQuery(id+"F11.imprint","IMPRINT",EDGE,{"derivedFrom":sQuery(id+"F11.wireOp",EDGE,"E13.1.14.0")}),-1.0]])]});
            var Q30;
            Q30=makeQuery(id+"F11.imprint","IMPRINT",FACE,{"disambiguationData":[TD([[makeQuery(id+"F11.imprint","IMPRINT",EDGE,{"derivedFrom":sQuery(id+"F11.wireOp",EDGE,"E13.1.15.0")}),-1.0]])]});
            var Q31;
            Q31=makeQuery(id+"F11.imprint","IMPRINT",FACE,{"disambiguationData":[TD([[makeQuery(id+"F11.imprint","IMPRINT",EDGE,{"derivedFrom":sQuery(id+"F11.wireOp",EDGE,"E13.1.16.0")}),-1.0]])]});
            extrude(context, id + "F12", {"entities" : qUnion([Q0, Q1, Q2, Q3, Q4, Q5, Q6, Q7, Q8, Q9, Q10, Q11, Q12, Q13, Q14, Q15, Q16, Q17, Q18, Q19, Q20, Q21, Q22, Q23, Q24, Q25, Q26, Q27, Q28, Q29, Q30, Q31]), "operationType" : NewBodyOperationType.REMOVE, "oppositeDirection" : true, "depth" : 10 * mm, "offsetDistance" : 25 * mm});
        }
        {
            var Q0;
            Q0=makeQuery(id+"F7.opExtrude","CAP_FACE",FACE,{"disambiguationData":[OSD([sQuery(id+"F6.wireOp",EDGE,"E9.bottom"),sQuery(id+"F6.wireOp",EDGE,"E9.top"),sQuery(id+"F6.wireOp",EDGE,"E9.left"),sQuery(id+"F6.wireOp",EDGE,"E9.right")])],"isStart":false});
            var sketch = newSketch(context, id + "F13", { "sketchPlane" : qUnion([Q0])});
            skLineSegment(sketch, "E14.bottom", {"start": v(98, -70) * mm, "end": v(88, -70) * mm});
            skLineSegment(sketch, "E14.top", {"start": v(98, -60) * mm, "end": v(88, -60) * mm});
            skLineSegment(sketch, "E14.left", {"start": v(98, -70) * mm, "end": v(98, -60) * mm});
            skLineSegment(sketch, "E14.right", {"start": v(88, -70) * mm, "end": v(88, -60) * mm});
            skLineSegment(sketch, "E15.MirrorCS", {"start": v(-88, -70) * mm, "end": v(-88, -60) * mm});
            skLineSegment(sketch, "E16.MirrorCS", {"start": v(-98, -70) * mm, "end": v(-88, -70) * mm});
            skLineSegment(sketch, "E17.MirrorCS", {"start": v(-98, -70) * mm, "end": v(-98, -60) * mm});
            skLineSegment(sketch, "E18.MirrorCS", {"start": v(-98, -60) * mm, "end": v(-88, -60) * mm});
            skLineSegment(sketch, "E19.bottom", {"start": v(98, 10) * mm, "end": v(88, 10) * mm});
            skLineSegment(sketch, "E19.top", {"start": v(98, 20) * mm, "end": v(88, 20) * mm});
            skLineSegment(sketch, "E19.left", {"start": v(98, 10) * mm, "end": v(98, 20) * mm});
            skLineSegment(sketch, "E19.right", {"start": v(88, 10) * mm, "end": v(88, 20) * mm});
            skLineSegment(sketch, "E20.MirrorCS", {"start": v(-98, 10) * mm, "end": v(-88, 10) * mm});
            skLineSegment(sketch, "E21.MirrorCS", {"start": v(-98, 20) * mm, "end": v(-88, 20) * mm});
            skLineSegment(sketch, "E22.MirrorCS", {"start": v(-88, 10) * mm, "end": v(-88, 20) * mm});
            skLineSegment(sketch, "E23.MirrorCS", {"start": v(-98, 10) * mm, "end": v(-98, 20) * mm});
            skSolve(sketch);
        }
        {
            var Q0;
            {var subQ4=sQuery(id+"F13.wireOp",EDGE,"E14.top");Q0=makeQuery(id+"F13.imprint","IMPRINT",FACE,{"disambiguationData":[TD([[makeQuery(id+"F13.imprint","IMPRINT",EDGE,{"derivedFrom":subQ4}),1.0]])]});}
            var Q1;
            {var subQ6=sQuery(id+"F13.wireOp",EDGE,"E15.MirrorCS");Q1=makeQuery(id+"F13.imprint","IMPRINT",FACE,{"disambiguationData":[TD([[makeQuery(id+"F13.imprint","IMPRINT",EDGE,{"derivedFrom":subQ6}),1.0]])]});}
            var Q2;
            Q2=makeQuery(id+"F13.imprint","IMPRINT",FACE,{"disambiguationData":[TD([[makeQuery(id+"F13.imprint","IMPRINT",EDGE,{"derivedFrom":sQuery(id+"F13.wireOp",EDGE,"E20.MirrorCS")}),1.0]])]});
            var Q3;
            Q3=makeQuery(id+"F13.imprint","IMPRINT",FACE,{"disambiguationData":[TD([[makeQuery(id+"F13.imprint","IMPRINT",EDGE,{"derivedFrom":sQuery(id+"F13.wireOp",EDGE,"E19.bottom")}),-1.0]])]});
            extrude(context, id + "F14", {"entities" : qUnion([Q0, Q1, Q2, Q3]), "operationType" : NewBodyOperationType.REMOVE, "oppositeDirection" : true, "depth" : 10 * mm, "offsetDistance" : 25 * mm});
        }
        {
            var Q0;
            Q0=makeQuery(id+"F14.boolean.opBoolean","COPY",FACE,{"derivedFrom":makeQuery(id+"F14.opExtrude","CAP_FACE",FACE,{"disambiguationData":[OSD([sQuery(id+"F2.wireOp",EDGE,"E1.bottom"),sQuery(id+"F2.wireOp",EDGE,"E1.left"),sQuery(id+"F6.wireOp",EDGE,"E9.bottom"),sQuery(id+"F6.wireOp",EDGE,"E9.top"),sQuery(id+"F6.wireOp",EDGE,"E9.left"),sQuery(id+"F6.wireOp",EDGE,"E9.right"),sQuery(id+"F13.wireOp",EDGE,"E14.bottom"),sQuery(id+"F13.wireOp",EDGE,"E14.top"),sQuery(id+"F13.wireOp",EDGE,"E14.left"),sQuery(id+"F13.wireOp",EDGE,"E14.right")])],"isStart":false})});
            var sketch = newSketch(context, id + "F15", { "sketchPlane" : qUnion([Q0])});
            skCircle(sketch, "E24", {"center": v(93, -65) * mm, "radius": 2.5 * mm});
            skCircle(sketch, "E25.MirrorC", {"center": v(-93, -65) * mm, "radius": 2.5 * mm});
            skCircle(sketch, "E26", {"center": v(93, 15) * mm, "radius": 2.5 * mm});
            skPoint(sketch, "E26.centerSnap0", {"position": v(93, -60) * mm});
            skCircle(sketch, "E27.MirrorC", {"center": v(-93, 15) * mm, "radius": 2.5 * mm});
            skSolve(sketch);
        }
        {
            var Q0;
            Q0=makeQuery(id+"F15.imprint","IMPRINT",FACE,{"disambiguationData":[TD([[makeQuery(id+"F15.imprint","IMPRINT",EDGE,{"derivedFrom":sQuery(id+"F15.wireOp",EDGE,"E24")}),1.0]])]});
            var Q1;
            Q1=makeQuery(id+"F15.imprint","IMPRINT",FACE,{"disambiguationData":[TD([[makeQuery(id+"F15.imprint","IMPRINT",EDGE,{"derivedFrom":sQuery(id+"F15.wireOp",EDGE,"E26")}),1.0]])]});
            var Q2;
            Q2=makeQuery(id+"F15.imprint","IMPRINT",FACE,{"disambiguationData":[TD([[makeQuery(id+"F15.imprint","IMPRINT",EDGE,{"derivedFrom":sQuery(id+"F15.wireOp",EDGE,"E25.MirrorC")}),-1.0]])]});
            var Q3;
            Q3=makeQuery(id+"F15.imprint","IMPRINT",FACE,{"disambiguationData":[TD([[makeQuery(id+"F15.imprint","IMPRINT",EDGE,{"derivedFrom":sQuery(id+"F15.wireOp",EDGE,"E27.MirrorC")}),-1.0]])]});
            extrude(context, id + "F16", {"entities" : qUnion([Q0, Q1, Q2, Q3]), "operationType" : NewBodyOperationType.REMOVE, "oppositeDirection" : true, "depth" : 20 * mm, "offsetDistance" : 25 * mm});
        }
        {
            var Q0;
            Q0=makeQuery(id+"F1.opExtrude","CAP_FACE",FACE,{"disambiguationData":[OSD([sQuery(id+"F0.wireOp",EDGE,"E0.bottom"),sQuery(id+"F0.wireOp",EDGE,"E0.top"),sQuery(id+"F0.wireOp",EDGE,"E0.left"),sQuery(id+"F0.wireOp",EDGE,"E0.right")])],"isStart":false});
            var sketch = newSketch(context, id + "F17", { "sketchPlane" : qUnion([Q0])});
            skLineSegment(sketch, "E28.bottom", {"start": v(-80, 60) * mm, "end": v(80, 60) * mm});
            skLineSegment(sketch, "E28.top", {"start": v(-80, -60) * mm, "end": v(80, -60) * mm});
            skLineSegment(sketch, "E28.left", {"start": v(-80, 60) * mm, "end": v(-80, -60) * mm});
            skLineSegment(sketch, "E28.right", {"start": v(80, 60) * mm, "end": v(80, -60) * mm});
            skPoint(sketch, "E28.middle", {"position": v(0, 0) * mm});
            skSolve(sketch);
        }
        {
            var Q0;
            Q0=makeQuery(id+"F17.imprint","IMPRINT",FACE,{"disambiguationData":[TD([[makeQuery(id+"F17.imprint","IMPRINT",EDGE,{"derivedFrom":sQuery(id+"F17.wireOp",EDGE,"E28.bottom")}),-1.0]])]});
            extrude(context, id + "F18", {"entities" : qUnion([Q0]), "operationType" : NewBodyOperationType.REMOVE, "oppositeDirection" : true, "depth" : 2 * mm, "offsetDistance" : 25 * mm});
        }
        {
            var Q0;
            Q0=makeQuery(id+"F18.boolean.opBoolean","COPY",FACE,{"derivedFrom":makeQuery(id+"F18.opExtrude","CAP_FACE",FACE,{"disambiguationData":[OSD([sQuery(id+"F17.wireOp",EDGE,"E28.bottom"),sQuery(id+"F17.wireOp",EDGE,"E28.top"),sQuery(id+"F17.wireOp",EDGE,"E28.left"),sQuery(id+"F17.wireOp",EDGE,"E28.right")])],"isStart":false})});
            var sketch = newSketch(context, id + "F19", { "sketchPlane" : qUnion([Q0])});
            skLineSegment(sketch, "E29.bottom", {"start": v(70, -50) * mm, "end": v(-70, -50) * mm});
            skLineSegment(sketch, "E29.top", {"start": v(70, 30) * mm, "end": v(-70, 30) * mm});
            skLineSegment(sketch, "E29.left", {"start": v(70, -50) * mm, "end": v(70, 30) * mm});
            skLineSegment(sketch, "E29.right", {"start": v(-70, -50) * mm, "end": v(-70, 30) * mm});
            skLineSegment(sketch, "E30.bottom", {"start": v(80, -60) * mm, "end": v(-80, -60) * mm});
            skLineSegment(sketch, "E30.top", {"start": v(80, 60) * mm, "end": v(-80, 60) * mm});
            skLineSegment(sketch, "E30.left", {"start": v(80, -60) * mm, "end": v(80, 60) * mm});
            skLineSegment(sketch, "E30.right", {"start": v(-80, -60) * mm, "end": v(-80, 60) * mm});
            skLineSegment(sketch, "E31.bottom", {"start": v(62.5, 60) * mm, "end": v(47.5, 60) * mm});
            skLineSegment(sketch, "E31.top", {"start": v(55.5, 45) * mm, "end": v(47.5, 45) * mm});
            skLineSegment(sketch, "E31.left", {"start": v(62.5, 60) * mm, "end": v(62.5, 45) * mm});
            skLineSegment(sketch, "E31.right", {"start": v(47.5, 60) * mm, "end": v(47.5, 45) * mm});
            skLineSegment(sketch, "E32.bottom", {"start": v(62.5, 48.5) * mm, "end": v(55.5, 48.5) * mm});
            skLineSegment(sketch, "E32.top", {"start": v(62.5, 41.5) * mm, "end": v(55.5, 41.5) * mm});
            skLineSegment(sketch, "E32.left", {"start": v(62.5, 48.5) * mm, "end": v(62.5, 41.5) * mm});
            skLineSegment(sketch, "E32.right", {"start": v(55.5, 48.5) * mm, "end": v(55.5, 41.5) * mm});
            skLineSegment(sketch, "E33.1.0.0", {"start": v(40.5, 60) * mm, "end": v(40.5, 45) * mm});
            skLineSegment(sketch, "E33.1.0.1", {"start": v(25.5, 60) * mm, "end": v(25.5, 45) * mm});
            skLineSegment(sketch, "E33.1.0.2", {"start": v(33.5, 45) * mm, "end": v(25.5, 45) * mm});
            skLineSegment(sketch, "E33.1.0.3", {"start": v(40.5, 41.5) * mm, "end": v(33.5, 41.5) * mm});
            skLineSegment(sketch, "E33.1.0.4", {"start": v(40.5, 48.5) * mm, "end": v(33.5, 48.5) * mm});
            skLineSegment(sketch, "E33.1.0.5", {"start": v(33.5, 48.5) * mm, "end": v(33.5, 41.5) * mm});
            skLineSegment(sketch, "E33.1.0.6", {"start": v(58, 60) * mm, "end": v(-102, 60) * mm});
            skLineSegment(sketch, "E33.2.0.0", {"start": v(18.5, 60) * mm, "end": v(18.5, 45) * mm});
            skLineSegment(sketch, "E33.2.0.1", {"start": v(3.5, 60) * mm, "end": v(3.5, 45) * mm});
            skLineSegment(sketch, "E33.2.0.2", {"start": v(11.5, 45) * mm, "end": v(3.5, 45) * mm});
            skLineSegment(sketch, "E33.2.0.3", {"start": v(18.5, 41.5) * mm, "end": v(11.5, 41.5) * mm});
            skLineSegment(sketch, "E33.2.0.4", {"start": v(18.5, 48.5) * mm, "end": v(11.5, 48.5) * mm});
            skLineSegment(sketch, "E33.2.0.5", {"start": v(11.5, 48.5) * mm, "end": v(11.5, 41.5) * mm});
            skLineSegment(sketch, "E33.2.0.6", {"start": v(36, 60) * mm, "end": v(-124, 60) * mm});
            skLineSegment(sketch, "E33.3.0.0", {"start": v(-3.5, 60) * mm, "end": v(-3.5, 45) * mm});
            skLineSegment(sketch, "E33.3.0.1", {"start": v(-18.5, 60) * mm, "end": v(-18.5, 45) * mm});
            skLineSegment(sketch, "E33.3.0.2", {"start": v(-10.5, 45) * mm, "end": v(-18.5, 45) * mm});
            skLineSegment(sketch, "E33.3.0.3", {"start": v(-3.5, 41.5) * mm, "end": v(-10.5, 41.5) * mm});
            skLineSegment(sketch, "E33.3.0.4", {"start": v(-3.5, 48.5) * mm, "end": v(-10.5, 48.5) * mm});
            skLineSegment(sketch, "E33.3.0.5", {"start": v(-10.5, 48.5) * mm, "end": v(-10.5, 41.5) * mm});
            skLineSegment(sketch, "E33.3.0.6", {"start": v(14, 60) * mm, "end": v(-146, 60) * mm});
            skLineSegment(sketch, "E33.4.0.0", {"start": v(-25.5, 60) * mm, "end": v(-25.5, 45) * mm});
            skLineSegment(sketch, "E33.4.0.1", {"start": v(-40.5, 60) * mm, "end": v(-40.5, 45) * mm});
            skLineSegment(sketch, "E33.4.0.2", {"start": v(-32.5, 45) * mm, "end": v(-40.5, 45) * mm});
            skLineSegment(sketch, "E33.4.0.3", {"start": v(-25.5, 41.5) * mm, "end": v(-32.5, 41.5) * mm});
            skLineSegment(sketch, "E33.4.0.4", {"start": v(-25.5, 48.5) * mm, "end": v(-32.5, 48.5) * mm});
            skLineSegment(sketch, "E33.4.0.5", {"start": v(-32.5, 48.5) * mm, "end": v(-32.5, 41.5) * mm});
            skLineSegment(sketch, "E33.4.0.6", {"start": v(-8, 60) * mm, "end": v(-168, 60) * mm});
            skLineSegment(sketch, "E33.5.0.0", {"start": v(-47.5, 60) * mm, "end": v(-47.5, 45) * mm});
            skLineSegment(sketch, "E33.5.0.1", {"start": v(-62.5, 60) * mm, "end": v(-62.5, 45) * mm});
            skLineSegment(sketch, "E33.5.0.2", {"start": v(-54.5, 45) * mm, "end": v(-62.5, 45) * mm});
            skLineSegment(sketch, "E33.5.0.3", {"start": v(-47.5, 41.5) * mm, "end": v(-54.5, 41.5) * mm});
            skLineSegment(sketch, "E33.5.0.4", {"start": v(-47.5, 48.5) * mm, "end": v(-54.5, 48.5) * mm});
            skLineSegment(sketch, "E33.5.0.5", {"start": v(-54.5, 48.5) * mm, "end": v(-54.5, 41.5) * mm});
            skLineSegment(sketch, "E33.5.0.6", {"start": v(-30, 60) * mm, "end": v(-190, 60) * mm});
            skLineSegment(sketch, "E33.direction1", {"start": v(62.5, 45) * mm, "end": v(40.5, 45) * mm, "construction": true});
            skLineSegment(sketch, "E34", {"start": v(40.5, 41.5) * mm, "end": v(40.5, 45) * mm});
            skLineSegment(sketch, "E35", {"start": v(18.5, 41.5) * mm, "end": v(18.5, 45) * mm});
            skLineSegment(sketch, "E36", {"start": v(-3.5, 41.5) * mm, "end": v(-3.5, 45) * mm});
            skLineSegment(sketch, "E37", {"start": v(-25.5, 41.5) * mm, "end": v(-25.5, 45) * mm});
            skLineSegment(sketch, "E38", {"start": v(-47.5, 41.5) * mm, "end": v(-47.5, 45) * mm});
            skSolve(sketch);
        }
        {
            var Q0;
            Q0=makeQuery(id+"F19.imprint","IMPRINT",FACE,{"disambiguationData":[TD([[makeQuery(id+"F19.imprint","IMPRINT",EDGE,{"derivedFrom":sQuery(id+"F19.wireOp",EDGE,"E29.bottom")}),-1.0]])]});
            var Q1;
            {var subQ3=sQuery(id+"F19.wireOp",EDGE,"E32.bottom");Q1=makeQuery(id+"F19.imprint","IMPRINT",FACE,{"disambiguationData":[TD([[makeQuery(id+"F19.imprint","IMPRINT",EDGE,{"derivedFrom":subQ3}),1.0]])]});}
            var Q2;
            {var subQ1=sQuery(id+"F19.wireOp",EDGE,"E33.1.0.3");Q2=makeQuery(id+"F19.imprint","IMPRINT",FACE,{"disambiguationData":[TD([[makeQuery(id+"F19.imprint","IMPRINT",EDGE,{"derivedFrom":subQ1}),-1.0]])]});}
            var Q3;
            {var subQ1=sQuery(id+"F19.wireOp",EDGE,"E33.2.0.3");Q3=makeQuery(id+"F19.imprint","IMPRINT",FACE,{"disambiguationData":[TD([[makeQuery(id+"F19.imprint","IMPRINT",EDGE,{"derivedFrom":subQ1}),-1.0]])]});}
            var Q4;
            {var subQ1=sQuery(id+"F19.wireOp",EDGE,"E33.3.0.3");Q4=makeQuery(id+"F19.imprint","IMPRINT",FACE,{"disambiguationData":[TD([[makeQuery(id+"F19.imprint","IMPRINT",EDGE,{"derivedFrom":subQ1}),-1.0]])]});}
            var Q5;
            {var subQ1=sQuery(id+"F19.wireOp",EDGE,"E33.4.0.3");Q5=makeQuery(id+"F19.imprint","IMPRINT",FACE,{"disambiguationData":[TD([[makeQuery(id+"F19.imprint","IMPRINT",EDGE,{"derivedFrom":subQ1}),-1.0]])]});}
            var Q6;
            {var subQ2=sQuery(id+"F19.wireOp",EDGE,"E33.5.0.3");Q6=makeQuery(id+"F19.imprint","IMPRINT",FACE,{"disambiguationData":[TD([[makeQuery(id+"F19.imprint","IMPRINT",EDGE,{"derivedFrom":subQ2}),-1.0]])]});}
            extrude(context, id + "F20", {"entities" : qUnion([Q0, Q1, Q2, Q3, Q4, Q5, Q6]), "operationType" : NewBodyOperationType.ADD, "depth" : 2 * mm, "offsetDistance" : 25 * mm});
        }
        {
            var Q0;
            Q0=makeQuery(id+"F18.boolean.opBoolean","COPY",FACE,{"derivedFrom":makeQuery(id+"F18.opExtrude","CAP_FACE",FACE,{"disambiguationData":[OSD([sQuery(id+"F17.wireOp",EDGE,"E28.bottom"),sQuery(id+"F17.wireOp",EDGE,"E28.top"),sQuery(id+"F17.wireOp",EDGE,"E28.left"),sQuery(id+"F17.wireOp",EDGE,"E28.right")])],"isStart":false})});
            var sketch = newSketch(context, id + "F21", { "sketchPlane" : qUnion([Q0])});
            skLineSegment(sketch, "E39", {"start": v(80, -60) * mm, "end": v(-80, -60) * mm});
            skLineSegment(sketch, "E40", {"start": v(-80, -60) * mm, "end": v(-80, 60) * mm});
            skLineSegment(sketch, "E41", {"start": v(-80, 60) * mm, "end": v(80, 60) * mm});
            skLineSegment(sketch, "E42", {"start": v(80, 60) * mm, "end": v(80, -60) * mm});
            skLineSegment(sketch, "E43", {"start": v(70, -50) * mm, "end": v(-70, -50) * mm});
            skLineSegment(sketch, "E44", {"start": v(-70, -50) * mm, "end": v(-70, 30) * mm});
            skLineSegment(sketch, "E45", {"start": v(-70, 30) * mm, "end": v(70, 30) * mm});
            skLineSegment(sketch, "E46", {"start": v(70, 30) * mm, "end": v(70, -50) * mm});
            skLineSegment(sketch, "E47", {"start": v(62.5, 48.5) * mm, "end": v(62.5, 60) * mm});
            skLineSegment(sketch, "E48", {"start": v(62.5, 60) * mm, "end": v(47.5, 60) * mm});
            skLineSegment(sketch, "E49", {"start": v(47.5, 60) * mm, "end": v(47.5, 45) * mm});
            skLineSegment(sketch, "E50", {"start": v(47.5, 45) * mm, "end": v(55.5, 45) * mm});
            skLineSegment(sketch, "E51", {"start": v(55.5, 45) * mm, "end": v(55.5, 48.5) * mm});
            skLineSegment(sketch, "E52", {"start": v(55.5, 48.5) * mm, "end": v(62.5, 48.5) * mm});
            skLineSegment(sketch, "E53.1.0.0", {"start": v(25.5, 45) * mm, "end": v(33.5, 45) * mm});
            skLineSegment(sketch, "E53.1.0.1", {"start": v(25.5, 60) * mm, "end": v(25.5, 45) * mm});
            skLineSegment(sketch, "E53.1.0.2", {"start": v(33.5, 48.5) * mm, "end": v(40.5, 48.5) * mm});
            skLineSegment(sketch, "E53.1.0.3", {"start": v(33.5, 45) * mm, "end": v(33.5, 48.5) * mm});
            skLineSegment(sketch, "E53.1.0.4", {"start": v(40.5, 48.5) * mm, "end": v(40.5, 60) * mm});
            skLineSegment(sketch, "E53.1.0.5", {"start": v(40.5, 60) * mm, "end": v(25.5, 60) * mm});
            skLineSegment(sketch, "E53.2.0.0", {"start": v(3.5, 45) * mm, "end": v(11.5, 45) * mm});
            skLineSegment(sketch, "E53.2.0.1", {"start": v(3.5, 60) * mm, "end": v(3.5, 45) * mm});
            skLineSegment(sketch, "E53.2.0.2", {"start": v(11.5, 48.5) * mm, "end": v(18.5, 48.5) * mm});
            skLineSegment(sketch, "E53.2.0.3", {"start": v(11.5, 45) * mm, "end": v(11.5, 48.5) * mm});
            skLineSegment(sketch, "E53.2.0.4", {"start": v(18.5, 48.5) * mm, "end": v(18.5, 60) * mm});
            skLineSegment(sketch, "E53.2.0.5", {"start": v(18.5, 60) * mm, "end": v(3.5, 60) * mm});
            skLineSegment(sketch, "E53.3.0.0", {"start": v(-18.5, 45) * mm, "end": v(-10.5, 45) * mm});
            skLineSegment(sketch, "E53.3.0.1", {"start": v(-18.5, 60) * mm, "end": v(-18.5, 45) * mm});
            skLineSegment(sketch, "E53.3.0.2", {"start": v(-10.5, 48.5) * mm, "end": v(-3.5, 48.5) * mm});
            skLineSegment(sketch, "E53.3.0.3", {"start": v(-10.5, 45) * mm, "end": v(-10.5, 48.5) * mm});
            skLineSegment(sketch, "E53.3.0.4", {"start": v(-3.5, 48.5) * mm, "end": v(-3.5, 60) * mm});
            skLineSegment(sketch, "E53.3.0.5", {"start": v(-3.5, 60) * mm, "end": v(-18.5, 60) * mm});
            skLineSegment(sketch, "E53.4.0.0", {"start": v(-40.5, 45) * mm, "end": v(-32.5, 45) * mm});
            skLineSegment(sketch, "E53.4.0.1", {"start": v(-40.5, 60) * mm, "end": v(-40.5, 45) * mm});
            skLineSegment(sketch, "E53.4.0.2", {"start": v(-32.5, 48.5) * mm, "end": v(-25.5, 48.5) * mm});
            skLineSegment(sketch, "E53.4.0.3", {"start": v(-32.5, 45) * mm, "end": v(-32.5, 48.5) * mm});
            skLineSegment(sketch, "E53.4.0.4", {"start": v(-25.5, 48.5) * mm, "end": v(-25.5, 60) * mm});
            skLineSegment(sketch, "E53.4.0.5", {"start": v(-25.5, 60) * mm, "end": v(-40.5, 60) * mm});
            skLineSegment(sketch, "E53.5.0.0", {"start": v(-62.5, 45) * mm, "end": v(-54.5, 45) * mm});
            skLineSegment(sketch, "E53.5.0.1", {"start": v(-62.5, 60) * mm, "end": v(-62.5, 45) * mm});
            skLineSegment(sketch, "E53.5.0.2", {"start": v(-54.5, 48.5) * mm, "end": v(-47.5, 48.5) * mm});
            skLineSegment(sketch, "E53.5.0.3", {"start": v(-54.5, 45) * mm, "end": v(-54.5, 48.5) * mm});
            skLineSegment(sketch, "E53.5.0.4", {"start": v(-47.5, 48.5) * mm, "end": v(-47.5, 60) * mm});
            skLineSegment(sketch, "E53.5.0.5", {"start": v(-47.5, 60) * mm, "end": v(-62.5, 60) * mm});
            skLineSegment(sketch, "E53.direction1", {"start": v(47.5, 45) * mm, "end": v(25.5, 45) * mm, "construction": true});
            skSolve(sketch);
        }
        {
            var Q0;
            Q0=makeQuery(id+"F21.imprint","IMPRINT",FACE,{"disambiguationData":[TD([[makeQuery(id+"F21.imprint","IMPRINT",EDGE,{"derivedFrom":sQuery(id+"F21.wireOp",EDGE,"E39")}),1.0]])]});
            extrude(context, id + "F22", {"entities" : qUnion([Q0]), "depth" : 2 * mm, "offsetDistance" : 25 * mm});
        }
        {
            var Q0;
            Q0=makeQuery(id+"F7.boolean.opBoolean","MERGE",FACE,{"derivedFrom":[makeQuery(id+"F3.opExtrude","SWEPT_FACE",FACE,{"disambiguationData":[OSD([sQuery(id+"F2.wireOp",EDGE,"E1.bottom")])]}),makeQuery(id+"F7.opExtrude","SWEPT_FACE",FACE,{"disambiguationData":[OSD([sQuery(id+"F6.wireOp",EDGE,"E9.bottom")])]})]});
            var sketch = newSketch(context, id + "F23", { "sketchPlane" : qUnion([Q0])});
            skLineSegment(sketch, "E54", {"start": v(88, 64) * mm, "end": v(2, 64) * mm});
            skLineSegment(sketch, "E55", {"start": v(88, 64) * mm, "end": v(88, 34) * mm});
            skLineSegment(sketch, "E56", {"start": v(-88, 64) * mm, "end": v(-88, 34) * mm});
            skLineSegment(sketch, "E57", {"start": v(-88, 34) * mm, "end": v(88, 34) * mm});
            skLineSegment(sketch, "E58.bottom", {"start": v(82, 64) * mm, "end": v(78, 64) * mm});
            skLineSegment(sketch, "E58.top", {"start": v(82, 52) * mm, "end": v(78, 52) * mm});
            skLineSegment(sketch, "E58.left", {"start": v(82, 64) * mm, "end": v(82, 52) * mm});
            skLineSegment(sketch, "E58.right", {"start": v(78, 64) * mm, "end": v(78, 52) * mm});
            skLineSegment(sketch, "E59.1.0.0", {"start": v(72, 64) * mm, "end": v(68, 64) * mm});
            skLineSegment(sketch, "E59.1.0.1", {"start": v(72, 64) * mm, "end": v(72, 52) * mm});
            skLineSegment(sketch, "E59.1.0.2", {"start": v(68, 64) * mm, "end": v(68, 52) * mm});
            skLineSegment(sketch, "E59.1.0.3", {"start": v(72, 52) * mm, "end": v(68, 52) * mm});
            skLineSegment(sketch, "E59.2.0.0", {"start": v(62, 64) * mm, "end": v(58, 64) * mm});
            skLineSegment(sketch, "E59.2.0.1", {"start": v(62, 64) * mm, "end": v(62, 52) * mm});
            skLineSegment(sketch, "E59.2.0.2", {"start": v(58, 64) * mm, "end": v(58, 52) * mm});
            skLineSegment(sketch, "E59.2.0.3", {"start": v(62, 52) * mm, "end": v(58, 52) * mm});
            skLineSegment(sketch, "E59.3.0.0", {"start": v(52, 64) * mm, "end": v(48, 64) * mm});
            skLineSegment(sketch, "E59.3.0.1", {"start": v(52, 64) * mm, "end": v(52, 52) * mm});
            skLineSegment(sketch, "E59.3.0.2", {"start": v(48, 64) * mm, "end": v(48, 52) * mm});
            skLineSegment(sketch, "E59.3.0.3", {"start": v(52, 52) * mm, "end": v(48, 52) * mm});
            skLineSegment(sketch, "E59.4.0.0", {"start": v(42, 64) * mm, "end": v(38, 64) * mm});
            skLineSegment(sketch, "E59.4.0.1", {"start": v(42, 64) * mm, "end": v(42, 52) * mm});
            skLineSegment(sketch, "E59.4.0.2", {"start": v(38, 64) * mm, "end": v(38, 52) * mm});
            skLineSegment(sketch, "E59.4.0.3", {"start": v(42, 52) * mm, "end": v(38, 52) * mm});
            skLineSegment(sketch, "E59.5.0.0", {"start": v(32, 64) * mm, "end": v(28, 64) * mm});
            skLineSegment(sketch, "E59.5.0.1", {"start": v(32, 64) * mm, "end": v(32, 52) * mm});
            skLineSegment(sketch, "E59.5.0.2", {"start": v(28, 64) * mm, "end": v(28, 52) * mm});
            skLineSegment(sketch, "E59.5.0.3", {"start": v(32, 52) * mm, "end": v(28, 52) * mm});
            skLineSegment(sketch, "E59.6.0.0", {"start": v(22, 64) * mm, "end": v(18, 64) * mm});
            skLineSegment(sketch, "E59.7.0.0", {"start": v(12, 64) * mm, "end": v(8, 64) * mm});
            skLineSegment(sketch, "E59.8.0.0", {"start": v(2, 64) * mm, "end": v(-2, 64) * mm});
            skLineSegment(sketch, "E59.9.0.0", {"start": v(-8, 64) * mm, "end": v(-12, 64) * mm});
            skLineSegment(sketch, "E59.10.0.0", {"start": v(-18, 64) * mm, "end": v(-22, 64) * mm});
            skLineSegment(sketch, "E59.11.0.0", {"start": v(-28, 64) * mm, "end": v(-32, 64) * mm});
            skLineSegment(sketch, "E59.11.0.1", {"start": v(-28, 64) * mm, "end": v(-28, 52) * mm});
            skLineSegment(sketch, "E59.11.0.2", {"start": v(-32, 64) * mm, "end": v(-32, 52) * mm});
            skLineSegment(sketch, "E59.11.0.3", {"start": v(-28, 52) * mm, "end": v(-32, 52) * mm});
            skLineSegment(sketch, "E59.12.0.0", {"start": v(-38, 64) * mm, "end": v(-42, 64) * mm});
            skLineSegment(sketch, "E59.12.0.1", {"start": v(-38, 64) * mm, "end": v(-38, 52) * mm});
            skLineSegment(sketch, "E59.12.0.2", {"start": v(-42, 64) * mm, "end": v(-42, 52) * mm});
            skLineSegment(sketch, "E59.12.0.3", {"start": v(-38, 52) * mm, "end": v(-42, 52) * mm});
            skLineSegment(sketch, "E59.13.0.0", {"start": v(-48, 64) * mm, "end": v(-52, 64) * mm});
            skLineSegment(sketch, "E59.13.0.1", {"start": v(-48, 64) * mm, "end": v(-48, 52) * mm});
            skLineSegment(sketch, "E59.13.0.2", {"start": v(-52, 64) * mm, "end": v(-52, 52) * mm});
            skLineSegment(sketch, "E59.13.0.3", {"start": v(-48, 52) * mm, "end": v(-52, 52) * mm});
            skLineSegment(sketch, "E59.14.0.0", {"start": v(-58, 64) * mm, "end": v(-62, 64) * mm});
            skLineSegment(sketch, "E59.14.0.1", {"start": v(-58, 64) * mm, "end": v(-58, 52) * mm});
            skLineSegment(sketch, "E59.14.0.2", {"start": v(-62, 64) * mm, "end": v(-62, 52) * mm});
            skLineSegment(sketch, "E59.14.0.3", {"start": v(-58, 52) * mm, "end": v(-62, 52) * mm});
            skLineSegment(sketch, "E59.15.0.0", {"start": v(-68, 64) * mm, "end": v(-72, 64) * mm});
            skLineSegment(sketch, "E59.15.0.1", {"start": v(-68, 64) * mm, "end": v(-68, 52) * mm});
            skLineSegment(sketch, "E59.15.0.2", {"start": v(-72, 64) * mm, "end": v(-72, 52) * mm});
            skLineSegment(sketch, "E59.15.0.3", {"start": v(-68, 52) * mm, "end": v(-72, 52) * mm});
            skLineSegment(sketch, "E59.16.0.0", {"start": v(-78, 64) * mm, "end": v(-82, 64) * mm});
            skLineSegment(sketch, "E59.16.0.1", {"start": v(-78, 64) * mm, "end": v(-78, 52) * mm});
            skLineSegment(sketch, "E59.16.0.2", {"start": v(-82, 64) * mm, "end": v(-82, 52) * mm});
            skLineSegment(sketch, "E59.16.0.3", {"start": v(-78, 52) * mm, "end": v(-82, 52) * mm});
            skLineSegment(sketch, "E59.direction1", {"start": v(78, 64) * mm, "end": v(68, 64) * mm, "construction": true});
            skLineSegment(sketch, "E60.trimOffspring", {"start": v(-2, 64) * mm, "end": v(-8, 64) * mm});
            skLineSegment(sketch, "E61.trimOffspring", {"start": v(-12, 64) * mm, "end": v(-88, 64) * mm});
            skSolve(sketch);
        }
        {
            var Q0;
            Q0=makeQuery(id+"F23.imprint","IMPRINT",FACE,{"disambiguationData":[TD([[makeQuery(id+"F23.imprint","IMPRINT",EDGE,{"derivedFrom":sQuery(id+"F23.wireOp",EDGE,"E58.top")}),-1.0]])]});
            var Q1;
            Q1=makeQuery(id+"F23.imprint","IMPRINT",FACE,{"disambiguationData":[TD([[makeQuery(id+"F23.imprint","IMPRINT",EDGE,{"derivedFrom":sQuery(id+"F23.wireOp",EDGE,"E59.1.0.0")}),1.0]])]});
            var Q2;
            Q2=makeQuery(id+"F23.imprint","IMPRINT",FACE,{"disambiguationData":[TD([[makeQuery(id+"F23.imprint","IMPRINT",EDGE,{"derivedFrom":sQuery(id+"F23.wireOp",EDGE,"E59.2.0.0")}),1.0]])]});
            var Q3;
            Q3=makeQuery(id+"F23.imprint","IMPRINT",FACE,{"disambiguationData":[TD([[makeQuery(id+"F23.imprint","IMPRINT",EDGE,{"derivedFrom":sQuery(id+"F23.wireOp",EDGE,"E59.3.0.0")}),1.0]])]});
            var Q4;
            Q4=makeQuery(id+"F23.imprint","IMPRINT",FACE,{"disambiguationData":[TD([[makeQuery(id+"F23.imprint","IMPRINT",EDGE,{"derivedFrom":sQuery(id+"F23.wireOp",EDGE,"E59.4.0.0")}),1.0]])]});
            var Q5;
            Q5=makeQuery(id+"F23.imprint","IMPRINT",FACE,{"disambiguationData":[TD([[makeQuery(id+"F23.imprint","IMPRINT",EDGE,{"derivedFrom":sQuery(id+"F23.wireOp",EDGE,"E59.5.0.0")}),1.0]])]});
            var Q6;
            {var subQ0=sQuery(id+"F23.wireOp",EDGE,"E59.11.0.1");Q6=makeQuery(id+"F23.imprint","IMPRINT",FACE,{"disambiguationData":[TD([[makeQuery(id+"F23.imprint","IMPRINT",EDGE,{"derivedFrom":subQ0}),-1.0]])]});}
            var Q7;
            {var subQ0=sQuery(id+"F23.wireOp",EDGE,"E59.12.0.1");Q7=makeQuery(id+"F23.imprint","IMPRINT",FACE,{"disambiguationData":[TD([[makeQuery(id+"F23.imprint","IMPRINT",EDGE,{"derivedFrom":subQ0}),-1.0]])]});}
            var Q8;
            {var subQ0=sQuery(id+"F23.wireOp",EDGE,"E59.13.0.1");Q8=makeQuery(id+"F23.imprint","IMPRINT",FACE,{"disambiguationData":[TD([[makeQuery(id+"F23.imprint","IMPRINT",EDGE,{"derivedFrom":subQ0}),-1.0]])]});}
            var Q9;
            {var subQ0=sQuery(id+"F23.wireOp",EDGE,"E59.14.0.1");Q9=makeQuery(id+"F23.imprint","IMPRINT",FACE,{"disambiguationData":[TD([[makeQuery(id+"F23.imprint","IMPRINT",EDGE,{"derivedFrom":subQ0}),-1.0]])]});}
            var Q10;
            {var subQ0=sQuery(id+"F23.wireOp",EDGE,"E59.15.0.1");Q10=makeQuery(id+"F23.imprint","IMPRINT",FACE,{"disambiguationData":[TD([[makeQuery(id+"F23.imprint","IMPRINT",EDGE,{"derivedFrom":subQ0}),-1.0]])]});}
            var Q11;
            {var subQ0=sQuery(id+"F23.wireOp",EDGE,"E59.16.0.1");Q11=makeQuery(id+"F23.imprint","IMPRINT",FACE,{"disambiguationData":[TD([[makeQuery(id+"F23.imprint","IMPRINT",EDGE,{"derivedFrom":subQ0}),-1.0]])]});}
            extrude(context, id + "F24", {"entities" : qUnion([Q0, Q1, Q2, Q3, Q4, Q5, Q6, Q7, Q8, Q9, Q10, Q11]), "operationType" : NewBodyOperationType.REMOVE, "oppositeDirection" : true, "depth" : 10 * mm, "offsetDistance" : 25 * mm});
        }
        {
            var Q0;
            Q0=makeQuery(id+"F1.opExtrude","CAP_FACE",FACE,{"disambiguationData":[OSD([sQuery(id+"F0.wireOp",EDGE,"E0.bottom"),sQuery(id+"F0.wireOp",EDGE,"E0.top"),sQuery(id+"F0.wireOp",EDGE,"E0.left"),sQuery(id+"F0.wireOp",EDGE,"E0.right")])],"isStart":false});
            var sketch = newSketch(context, id + "F25", { "sketchPlane" : qUnion([Q0])});
            skText(sketch, "E62", { "text": "SIMATIC PANEL", "fontName": "Tinos-Regular.ttf"});
            const initialGuessF25  = {"E62": [-0.07805, -0.12813, 1, 0, 0.004]};
            skSetInitialGuess(sketch, initialGuessF25);
            skSolve(sketch);
        }
        {
            var Q0;
            Q0 = qSketchRegion(id + "F25", true);
            extrude(context, id + "F26", {"entities" : qUnion([Q0]), "depth" : 1 * mm, "offsetDistance" : 25 * mm});
        }
        {
            var Q0;
            Q0=makeQuery(id+"F1.opExtrude","CAP_FACE",FACE,{"disambiguationData":[OSD([sQuery(id+"F0.wireOp",EDGE,"E0.bottom"),sQuery(id+"F0.wireOp",EDGE,"E0.top"),sQuery(id+"F0.wireOp",EDGE,"E0.left"),sQuery(id+"F0.wireOp",EDGE,"E0.right")])],"isStart":false});
            var sketch = newSketch(context, id + "F27", { "sketchPlane" : qUnion([Q0])});
            skText(sketch, "E63", { "text": "TOUCH", "fontName": "OpenSans-Bold.ttf"});
            const initialGuessF27  = {"E63": [-0.2482, -0.0002, 1, 0, 0.02]};
            skSetInitialGuess(sketch, initialGuessF27);
            skSolve(sketch);
        }
        {
            var Q0;
            Q0 = qSketchRegion(id + "F27", true);
            extrude(context, id + "F28", {"entities" : qUnion([Q0]), "depth" : 1 * mm, "offsetDistance" : 25 * mm});
        }
        {
            var Q0;
            Q0=makeQuery(id+"F1.opExtrude","CAP_FACE",FACE,{"disambiguationData":[OSD([sQuery(id+"F0.wireOp",EDGE,"E0.bottom"),sQuery(id+"F0.wireOp",EDGE,"E0.top"),sQuery(id+"F0.wireOp",EDGE,"E0.left"),sQuery(id+"F0.wireOp",EDGE,"E0.right")])],"isStart":false});
            var sketch = newSketch(context, id + "F29", { "sketchPlane" : qUnion([Q0])});
            skText(sketch, "E64", { "text": "SIAMENS", "fontName": "OpenSans-Regular.ttf"});
            skLineSegment(sketch, "E65", {"start": v(3.62, -142.96) * mm, "end": v(3.62, -139.96) * mm});
            skLineSegment(sketch, "E66", {"start": v(-14.04, -139.96) * mm, "end": v(-14.04, -142.96) * mm});
            const initialGuessF29  = {"E64": [-0.01404, -0.14296, 1, 0, 0.003]};
            skSetInitialGuess(sketch, initialGuessF29);
            skSolve(sketch);
        }
        {
            var Q0;
            Q0 = qSketchRegion(id + "F29", true);
            extrude(context, id + "F30", {"entities" : qUnion([Q0]), "depth" : 1 * mm, "offsetDistance" : 25 * mm});
        }
        {
            var Q0;
            Q0=makeQuery(id+"F30.opExtrude","CAP_FACE",FACE,{"disambiguationData":[OSD([sQuery(id+"F29.wireOp",EDGE,"E64.sketch_text.stroke-0"),sQuery(id+"F29.wireOp",EDGE,"E64.sketch_text.stroke-1"),sQuery(id+"F29.wireOp",EDGE,"E64.sketch_text.stroke-2"),sQuery(id+"F29.wireOp",EDGE,"E64.sketch_text.stroke-3"),sQuery(id+"F29.wireOp",EDGE,"E64.sketch_text.stroke-4"),sQuery(id+"F29.wireOp",EDGE,"E64.sketch_text.stroke-5"),sQuery(id+"F29.wireOp",EDGE,"E64.sketch_text.stroke-6"),sQuery(id+"F29.wireOp",EDGE,"E64.sketch_text.stroke-7"),sQuery(id+"F29.wireOp",EDGE,"E64.sketch_text.stroke-8"),sQuery(id+"F29.wireOp",EDGE,"E64.sketch_text.stroke-9"),sQuery(id+"F29.wireOp",EDGE,"E64.sketch_text.stroke-10"),sQuery(id+"F29.wireOp",EDGE,"E64.sketch_text.stroke-11"),sQuery(id+"F29.wireOp",EDGE,"E64.sketch_text.stroke-12"),sQuery(id+"F29.wireOp",EDGE,"E64.sketch_text.stroke-13"),sQuery(id+"F29.wireOp",EDGE,"E64.sketch_text.stroke-14"),sQuery(id+"F29.wireOp",EDGE,"E64.sketch_text.stroke-15"),sQuery(id+"F29.wireOp",EDGE,"E64.sketch_text.stroke-16"),sQuery(id+"F29.wireOp",EDGE,"E64.sketch_text.stroke-17"),sQuery(id+"F29.wireOp",EDGE,"E64.sketch_text.stroke-18"),sQuery(id+"F29.wireOp",EDGE,"E64.sketch_text.stroke-19"),sQuery(id+"F29.wireOp",EDGE,"E64.sketch_text.stroke-20"),sQuery(id+"F29.wireOp",EDGE,"E64.sketch_text.stroke-21"),sQuery(id+"F29.wireOp",EDGE,"E64.sketch_text.stroke-22"),sQuery(id+"F29.wireOp",EDGE,"E64.sketch_text.stroke-23"),sQuery(id+"F29.wireOp",EDGE,"E64.sketch_text.stroke-24")])],"isStart":true});
            var sketch = newSketch(context, id + "F31", { "sketchPlane" : qUnion([Q0])});
            skLineSegment(sketch, "E67.bottom", {"start": v(-4.62, -138.9) * mm, "end": v(15.38, -138.9) * mm});
            skLineSegment(sketch, "E67.top", {"start": v(-4.62, -143.9) * mm, "end": v(15.38, -143.9) * mm});
            skLineSegment(sketch, "E67.left", {"start": v(-4.62, -138.9) * mm, "end": v(-4.62, -143.9) * mm});
            skLineSegment(sketch, "E67.right", {"start": v(15.38, -138.9) * mm, "end": v(15.38, -143.9) * mm});
            skSolve(sketch);
        }
        {
            var Q0;
            Q0=makeQuery(id+"F31.imprint","IMPRINT",FACE,{"disambiguationData":[TD([[makeQuery(id+"F31.imprint","IMPRINT",EDGE,{"derivedFrom":sQuery(id+"F31.wireOp",EDGE,"E67.bottom")}),-1.0]])]});
            extrude(context, id + "F32", {"entities" : qUnion([Q0]), "oppositeDirection" : true, "depth" : 1 * mm, "offsetDistance" : 25 * mm});
        }
    });